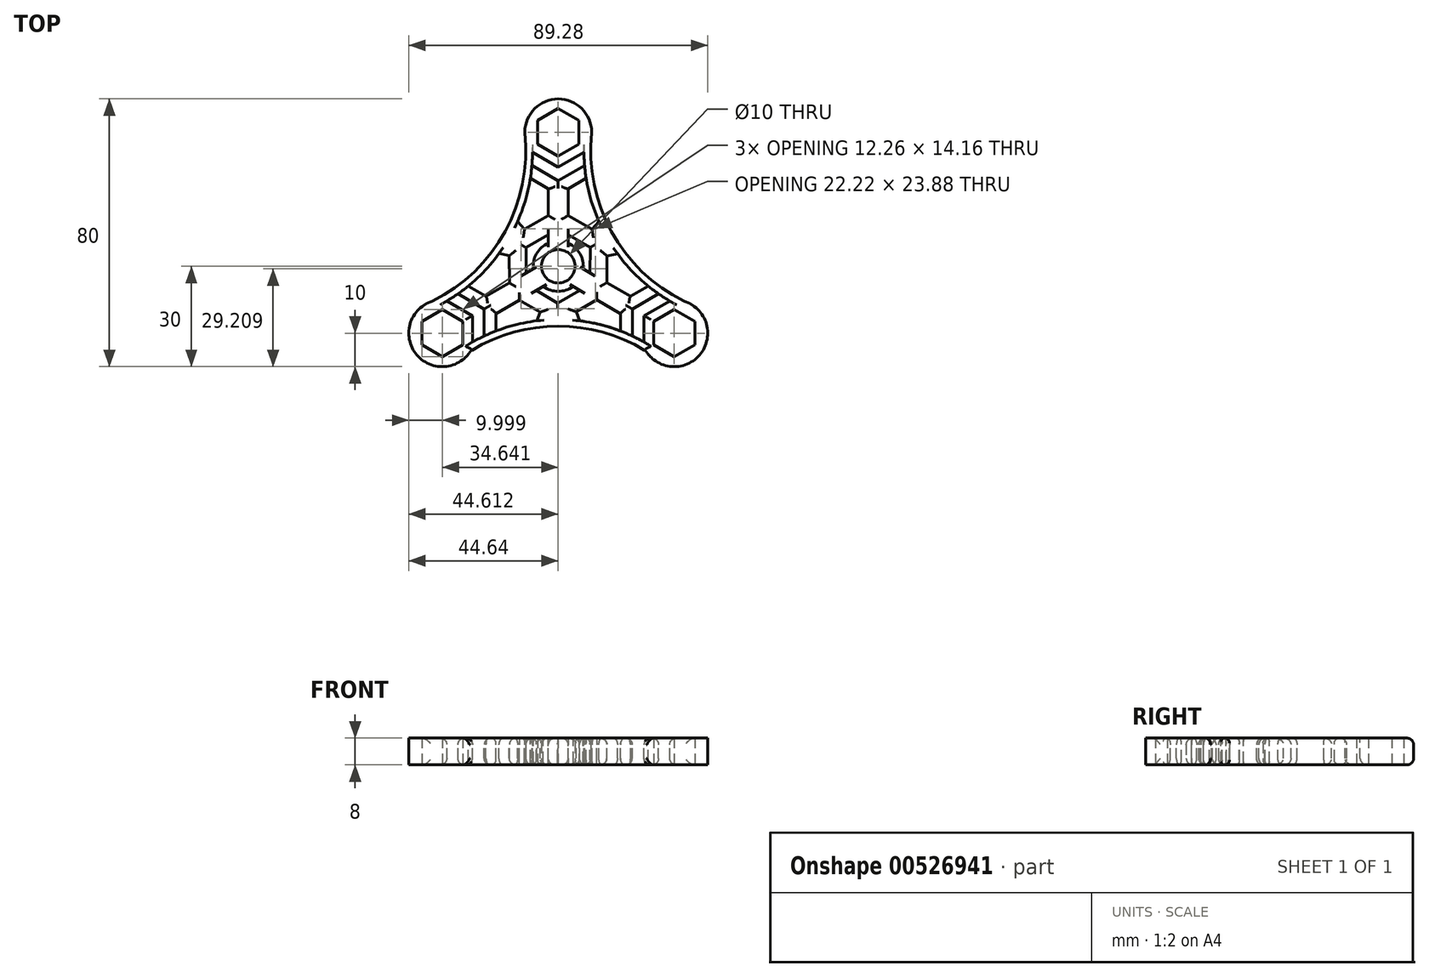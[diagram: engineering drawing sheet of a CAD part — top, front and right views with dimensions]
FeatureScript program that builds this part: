
annotation { "Feature Type Name" : "Feature", "Feature Type Description" : "" }
export const myFeature = defineFeature(function(context is Context, id is Id, definition is map)
    precondition{}
    {
        {
            var Q0;
            Q0=qCreatedBy(makeId("Top.planeOp"),FACE);
            var sketch = newSketch(context, id + "F0", { "sketchPlane" : qUnion([Q0])});
            skCircle(sketch, "E0", {"center": v(0, 0) * mm, "radius": 5 * mm});
            skLineSegment(sketch, "E1.0", {"start": v(-23.24, 13.42) * mm, "end": v(23.24, 13.42) * mm});
            skLineSegment(sketch, "E1.1", {"start": v(23.24, 13.42) * mm, "end": v(0, -26.83) * mm});
            skLineSegment(sketch, "E1.2", {"start": v(0, -26.83) * mm, "end": v(-23.24, 13.42) * mm});
            skPoint(sketch, "E1.0.midPoint", {"position": v(0, 13.42) * mm});
            skLineSegment(sketch, "E2", {"start": v(0, 0) * mm, "end": v(0, 40) * mm});
            skLineSegment(sketch, "E3", {"start": v(0, 0) * mm, "end": v(-34.64, -20) * mm});
            skLineSegment(sketch, "E4", {"start": v(0, 0) * mm, "end": v(34.64, -20) * mm});
            skCircle(sketch, "E5.cCircle", {"center": v(0, 40) * mm, "radius": 6.13 * mm, "construction": true});
            skLineSegment(sketch, "E5.0", {"start": v(-6.13, 36.46) * mm, "end": v(-6.13, 43.54) * mm});
            skLineSegment(sketch, "E5.1", {"start": v(-6.13, 43.54) * mm, "end": v(0, 47.08) * mm});
            skLineSegment(sketch, "E5.2", {"start": v(0, 47.08) * mm, "end": v(6.13, 43.54) * mm});
            skLineSegment(sketch, "E5.3", {"start": v(6.13, 43.54) * mm, "end": v(6.13, 36.46) * mm});
            skLineSegment(sketch, "E5.4", {"start": v(6.13, 36.46) * mm, "end": v(0, 32.92) * mm});
            skLineSegment(sketch, "E5.5", {"start": v(0, 32.92) * mm, "end": v(-6.13, 36.46) * mm});
            skPoint(sketch, "E5.0.midPoint", {"position": v(-6.13, 40) * mm});
            skCircle(sketch, "E6.cCircle", {"center": v(-34.64, -20) * mm, "radius": 6.13 * mm, "construction": true});
            skLineSegment(sketch, "E6.0", {"start": v(-40.77, -23.54) * mm, "end": v(-40.77, -16.46) * mm});
            skLineSegment(sketch, "E6.1", {"start": v(-40.77, -16.46) * mm, "end": v(-34.64, -12.92) * mm});
            skLineSegment(sketch, "E6.2", {"start": v(-34.64, -12.92) * mm, "end": v(-28.51, -16.46) * mm});
            skLineSegment(sketch, "E6.3", {"start": v(-28.51, -16.46) * mm, "end": v(-28.51, -23.54) * mm});
            skLineSegment(sketch, "E6.4", {"start": v(-28.51, -23.54) * mm, "end": v(-34.64, -27.08) * mm});
            skLineSegment(sketch, "E6.5", {"start": v(-34.64, -27.08) * mm, "end": v(-40.77, -23.54) * mm});
            skPoint(sketch, "E6.0.midPoint", {"position": v(-40.77, -20) * mm});
            skCircle(sketch, "E7.cCircle", {"center": v(34.64, -20) * mm, "radius": 6.13 * mm, "construction": true});
            skLineSegment(sketch, "E7.0", {"start": v(40.77, -16.46) * mm, "end": v(40.77, -23.54) * mm});
            skLineSegment(sketch, "E7.1", {"start": v(40.77, -23.54) * mm, "end": v(34.64, -27.08) * mm});
            skLineSegment(sketch, "E7.2", {"start": v(34.64, -27.08) * mm, "end": v(28.51, -23.54) * mm});
            skLineSegment(sketch, "E7.3", {"start": v(28.51, -23.54) * mm, "end": v(28.51, -16.46) * mm});
            skLineSegment(sketch, "E7.4", {"start": v(28.51, -16.46) * mm, "end": v(34.64, -12.92) * mm});
            skLineSegment(sketch, "E7.5", {"start": v(34.64, -12.92) * mm, "end": v(40.77, -16.46) * mm});
            skPoint(sketch, "E7.0.midPoint", {"position": v(40.77, -20) * mm});
            skCircle(sketch, "E8", {"center": v(0, 40) * mm, "radius": 10 * mm});
            skCircle(sketch, "E9", {"center": v(-34.64, -20) * mm, "radius": 10 * mm});
            skCircle(sketch, "E10", {"center": v(34.64, -20) * mm, "radius": 10 * mm});
            skArc(sketch, "E11", {"start": v(-37.7, -10.48) * mm, "mid": v(-15.86, 10.37) * mm, "end": v(-10, 40) * mm});
            skPoint(sketch, "E11.startSnap0", {"position": v(-37.7, -14.7) * mm});
            skPoint(sketch, "E12.startSnap0", {"position": v(31.58, -25.3) * mm});
            skPoint(sketch, "E12.endSnap0", {"position": v(-31.58, -25.3) * mm});
            skArc(sketch, "E13", {"start": v(10, 40) * mm, "mid": v(15.86, 10.37) * mm, "end": v(37.7, -10.48) * mm});
            skPoint(sketch, "E13.startSnap0", {"position": v(6.13, 40) * mm});
            skPoint(sketch, "E13.endSnap0", {"position": v(37.7, -14.7) * mm});
            skArc(sketch, "E14", {"start": v(26.17, -25.3) * mm, "mid": v(0, -17.92) * mm, "end": v(-26.17, -25.3) * mm});
            skSolve(sketch);
        }
        {
            var Q0;
            {var subQ0=sQuery(id+"F0.wireOp",EDGE,"E11");var subQ1=sQuery(id+"F0.wireOp",EDGE,"E1.0");var subQ2=makeQuery(id+"F0.imprint","INTERSECT",VERTEX,{"derivedFrom":[subQ1,subQ0]});Q0=makeQuery(id+"F0.imprint","IMPRINT",FACE,{"disambiguationData":[TD([[makeQuery(id+"F0.imprint","IMPRINT",EDGE,{"disambiguationData":[TD([[subQ2,-1.0]])],"derivedFrom":subQ1}),1.0]])]});}
            var Q1;
            Q1=makeQuery(id+"F0.imprint","IMPRINT",FACE,{"disambiguationData":[TD([[makeQuery(id+"F0.imprint","IMPRINT",EDGE,{"derivedFrom":sQuery(id+"F0.wireOp",EDGE,"E5.0")}),1.0]])]});
            var Q2;
            {var subQ0=sQuery(id+"F0.wireOp",EDGE,"E13");var subQ1=sQuery(id+"F0.wireOp",EDGE,"E1.0");var subQ2=makeQuery(id+"F0.imprint","INTERSECT",VERTEX,{"derivedFrom":[subQ1,subQ0]});Q2=makeQuery(id+"F0.imprint","IMPRINT",FACE,{"disambiguationData":[TD([[makeQuery(id+"F0.imprint","IMPRINT",EDGE,{"disambiguationData":[TD([[subQ2,1.0]])],"derivedFrom":subQ1}),1.0]])]});}
            var Q3;
            {var subQ1=sQuery(id+"F0.wireOp",EDGE,"E0");var subQ8=sQuery(id+"F0.wireOp",EDGE,"E3");var subQ11=makeQuery(id+"F0.imprint","INTERSECT",VERTEX,{"derivedFrom":[subQ1,subQ8]});Q3=makeQuery(id+"F0.imprint","IMPRINT",FACE,{"disambiguationData":[TD([[makeQuery(id+"F0.imprint","IMPRINT",EDGE,{"disambiguationData":[TD([[subQ11,1.0]])],"derivedFrom":subQ1}),-1.0]])]});}
            var Q4;
            {var subQ0=sQuery(id+"F0.wireOp",EDGE,"E2");var subQ1=sQuery(id+"F0.wireOp",EDGE,"E0");var subQ2=makeQuery(id+"F0.imprint","INTERSECT",VERTEX,{"derivedFrom":[subQ1,subQ0]});Q4=makeQuery(id+"F0.imprint","IMPRINT",FACE,{"disambiguationData":[TD([[makeQuery(id+"F0.imprint","IMPRINT",EDGE,{"disambiguationData":[TD([[subQ2,1.0]])],"derivedFrom":subQ1}),-1.0]])]});}
            var Q5;
            {var subQ3=sQuery(id+"F0.wireOp",EDGE,"E3");var subQ5=sQuery(id+"F0.wireOp",EDGE,"E0");var subQ6=makeQuery(id+"F0.imprint","INTERSECT",VERTEX,{"derivedFrom":[subQ5,subQ3]});Q5=makeQuery(id+"F0.imprint","IMPRINT",FACE,{"disambiguationData":[TD([[makeQuery(id+"F0.imprint","IMPRINT",EDGE,{"disambiguationData":[TD([[subQ6,-1.0]])],"derivedFrom":subQ5}),-1.0]])]});}
            var Q6;
            {var subQ0=sQuery(id+"F0.wireOp",EDGE,"E12");var subQ1=sQuery(id+"F0.wireOp",EDGE,"E1.2");var subQ2=makeQuery(id+"F0.imprint","INTERSECT",VERTEX,{"derivedFrom":[subQ1,subQ0]});Q6=makeQuery(id+"F0.imprint","IMPRINT",FACE,{"disambiguationData":[TD([[makeQuery(id+"F0.imprint","IMPRINT",EDGE,{"disambiguationData":[TD([[subQ2,-1.0]])],"derivedFrom":subQ1}),1.0]])]});}
            var Q7;
            {var subQ0=sQuery(id+"F0.wireOp",EDGE,"E11");var subQ1=sQuery(id+"F0.wireOp",EDGE,"E1.2");var subQ2=makeQuery(id+"F0.imprint","INTERSECT",VERTEX,{"derivedFrom":[subQ1,subQ0]});Q7=makeQuery(id+"F0.imprint","IMPRINT",FACE,{"disambiguationData":[TD([[makeQuery(id+"F0.imprint","IMPRINT",EDGE,{"disambiguationData":[TD([[subQ2,1.0]])],"derivedFrom":subQ1}),1.0]])]});}
            var Q8;
            Q8=makeQuery(id+"F0.imprint","IMPRINT",FACE,{"disambiguationData":[TD([[makeQuery(id+"F0.imprint","IMPRINT",EDGE,{"derivedFrom":sQuery(id+"F0.wireOp",EDGE,"E6.0")}),1.0]])]});
            var Q9;
            {var subQ0=sQuery(id+"F0.wireOp",EDGE,"E12");var subQ1=sQuery(id+"F0.wireOp",EDGE,"E1.1");var subQ2=makeQuery(id+"F0.imprint","INTERSECT",VERTEX,{"derivedFrom":[subQ1,subQ0]});Q9=makeQuery(id+"F0.imprint","IMPRINT",FACE,{"disambiguationData":[TD([[makeQuery(id+"F0.imprint","IMPRINT",EDGE,{"disambiguationData":[TD([[subQ2,1.0]])],"derivedFrom":subQ1}),1.0]])]});}
            var Q10;
            {var subQ0=sQuery(id+"F0.wireOp",EDGE,"E13");var subQ1=sQuery(id+"F0.wireOp",EDGE,"E1.1");var subQ2=makeQuery(id+"F0.imprint","INTERSECT",VERTEX,{"derivedFrom":[subQ1,subQ0]});Q10=makeQuery(id+"F0.imprint","IMPRINT",FACE,{"disambiguationData":[TD([[makeQuery(id+"F0.imprint","IMPRINT",EDGE,{"disambiguationData":[TD([[subQ2,-1.0]])],"derivedFrom":subQ1}),1.0]])]});}
            var Q11;
            Q11=makeQuery(id+"F0.imprint","IMPRINT",FACE,{"disambiguationData":[TD([[makeQuery(id+"F0.imprint","IMPRINT",EDGE,{"derivedFrom":sQuery(id+"F0.wireOp",EDGE,"E7.0")}),1.0]])]});
            extrude(context, id + "F1", {"entities" : qUnion([Q0, Q1, Q2, Q3, Q4, Q5, Q6, Q7, Q8, Q9, Q10, Q11]), "depth" : 8 * mm, "offsetDistance" : 25 * mm});
        }
        {
            var Q0;
            Q0=makeQuery(id+"F1.opExtrude","SWEPT_FACE",FACE,{"disambiguationData":[OSD([sQuery(id+"F0.wireOp",EDGE,"E14")])]});
            var Q1;
            Q1=makeQuery(id+"F1.opExtrude","SWEPT_FACE",FACE,{"disambiguationData":[OSD([sQuery(id+"F0.wireOp",EDGE,"E11")])]});
            var Q2;
            Q2=makeQuery(id+"F1.opExtrude","SWEPT_FACE",FACE,{"disambiguationData":[OSD([sQuery(id+"F0.wireOp",EDGE,"E13")])]});
            var Q3;
            Q3=makeQuery(id+"F1.opExtrude","SWEPT_FACE",FACE,{"disambiguationData":[OSD([sQuery(id+"F0.wireOp",EDGE,"E8")])]});
            fillet(context, id + "F2", {"entities" : qUnion([Q0, Q1, Q2, Q3]), "radius" : 2 * mm, "tangentPropagation" : true, "allowEdgeOverflow" : false});
        }
        {
            var Q0;
            Q0=makeQuery(id+"F1.opExtrude","CAP_FACE",FACE,{"disambiguationData":[OSD([sQuery(id+"F0.wireOp",EDGE,"E0"),sQuery(id+"F0.wireOp",EDGE,"E5.0"),sQuery(id+"F0.wireOp",EDGE,"E5.1"),sQuery(id+"F0.wireOp",EDGE,"E5.2"),sQuery(id+"F0.wireOp",EDGE,"E5.3"),sQuery(id+"F0.wireOp",EDGE,"E5.4"),sQuery(id+"F0.wireOp",EDGE,"E5.5"),sQuery(id+"F0.wireOp",EDGE,"E6.0"),sQuery(id+"F0.wireOp",EDGE,"E6.1"),sQuery(id+"F0.wireOp",EDGE,"E6.2"),sQuery(id+"F0.wireOp",EDGE,"E6.3"),sQuery(id+"F0.wireOp",EDGE,"E6.4"),sQuery(id+"F0.wireOp",EDGE,"E6.5"),sQuery(id+"F0.wireOp",EDGE,"E7.0"),sQuery(id+"F0.wireOp",EDGE,"E7.1"),sQuery(id+"F0.wireOp",EDGE,"E7.2"),sQuery(id+"F0.wireOp",EDGE,"E7.3"),sQuery(id+"F0.wireOp",EDGE,"E7.4"),sQuery(id+"F0.wireOp",EDGE,"E7.5"),sQuery(id+"F0.wireOp",EDGE,"E8"),sQuery(id+"F0.wireOp",EDGE,"E9"),sQuery(id+"F0.wireOp",EDGE,"E10"),sQuery(id+"F0.wireOp",EDGE,"E11"),sQuery(id+"F0.wireOp",EDGE,"E13"),sQuery(id+"F0.wireOp",EDGE,"E14")])],"isStart":false});
            var sketch = newSketch(context, id + "F3", { "sketchPlane" : qUnion([Q0])});
            skLineSegment(sketch, "E15.0", {"start": v(6.13, 36.46) * mm, "end": v(0, 32.92) * mm});
            skLineSegment(sketch, "E15.1", {"start": v(0, 32.92) * mm, "end": v(-6.13, 36.46) * mm});
            skLineSegment(sketch, "E16.0", {"start": v(0, 29.57) * mm, "end": v(-7.7, 34.01) * mm});
            skLineSegment(sketch, "E16.1", {"start": v(7.7, 34.01) * mm, "end": v(0, 29.57) * mm});
            skArc(sketch, "E17.0", {"start": v(36.7, -12.21) * mm, "mid": v(14.1, 9.42) * mm, "end": v(8, 40.1) * mm});
            skArc(sketch, "E17.1", {"start": v(-8, 40.1) * mm, "mid": v(-14.1, 9.42) * mm, "end": v(-36.7, -12.21) * mm});
            skLineSegment(sketch, "E18.0", {"start": v(0, 25.53) * mm, "end": v(-7.87, 30.08) * mm});
            skLineSegment(sketch, "E18.1", {"start": v(7.87, 30.08) * mm, "end": v(0, 25.53) * mm});
            skLineSegment(sketch, "E19.0", {"start": v(-3, 23.22) * mm, "end": v(-8.33, 26.3) * mm});
            skLineSegment(sketch, "E19.1", {"start": v(8.33, 26.3) * mm, "end": v(3, 23.22) * mm});
            skLineSegment(sketch, "E20.0", {"start": v(3, 9.42) * mm, "end": v(9.57, 5.65) * mm});
            skLineSegment(sketch, "E20.1", {"start": v(9.57, 5.65) * mm, "end": v(9.5, -2.02) * mm});
            skLineSegment(sketch, "E20.2", {"start": v(9.48, -5.44) * mm, "end": v(9.45, -5.46) * mm});
            skLineSegment(sketch, "E20.3", {"start": v(-0.15, -11) * mm, "end": v(-6.6, -7.27) * mm});
            skLineSegment(sketch, "E20.4", {"start": v(-9.61, -2.09) * mm, "end": v(-9.63, 5.57) * mm});
            skLineSegment(sketch, "E20.5", {"start": v(-9.63, 5.57) * mm, "end": v(-3, 9.4) * mm});
            skLineSegment(sketch, "E21.0", {"start": v(-14.6, -4.97) * mm, "end": v(-14.63, 3.14) * mm});
            skLineSegment(sketch, "E21.1", {"start": v(3, 15.18) * mm, "end": v(10.09, 11.12) * mm});
            skLineSegment(sketch, "E21.2", {"start": v(14.55, 3.08) * mm, "end": v(14.48, -4.9) * mm});
            skLineSegment(sketch, "E21.3", {"start": v(-10.07, 11.1) * mm, "end": v(-3, 15.17) * mm});
            skLineSegment(sketch, "E21.4", {"start": v(11.45, -10.08) * mm, "end": v(5.37, -13.59) * mm});
            skArc(sketch, "E22", {"start": v(-3, 6.87) * mm, "mid": v(-6.5, 3.75) * mm, "end": v(-7.45, -0.84) * mm});
            skLineSegment(sketch, "E23.right", {"start": v(3, 6.87) * mm, "end": v(3, 9.42) * mm});
            skLineSegment(sketch, "E24.right", {"start": v(-3, 6.87) * mm, "end": v(-3, 9.4) * mm});
            skLineSegment(sketch, "E25.trimOffspring", {"start": v(3, 15.18) * mm, "end": v(3, 23.22) * mm});
            skLineSegment(sketch, "E26.trimOffspring", {"start": v(-3, 15.17) * mm, "end": v(-3, 23.22) * mm});
            skLineSegment(sketch, "E27.trimOffspring", {"start": v(0, 25.53) * mm, "end": v(0, 29.57) * mm});
            skLineSegment(sketch, "E28.trimOffspring", {"start": v(0, 25.53) * mm, "end": v(0, 40) * mm});
            skLineSegment(sketch, "E29.trimOffspring", {"start": v(0, 11.13) * mm, "end": v(0, 11.14) * mm});
            skLineSegment(sketch, "E30.0", {"start": v(-25.61, -14.79) * mm, "end": v(-25.61, -22.66) * mm});
            skLineSegment(sketch, "E30.1", {"start": v(-33.27, -10.36) * mm, "end": v(-25.61, -14.79) * mm});
            skLineSegment(sketch, "E31.0", {"start": v(-22.11, -12.77) * mm, "end": v(-22.11, -20.85) * mm});
            skLineSegment(sketch, "E31.1", {"start": v(-29.96, -8.24) * mm, "end": v(-22.11, -12.77) * mm});
            skLineSegment(sketch, "E32.0", {"start": v(-18.61, -10.75) * mm, "end": v(-18.61, -19.36) * mm});
            skLineSegment(sketch, "E32.1", {"start": v(-26.92, -5.95) * mm, "end": v(-18.61, -10.75) * mm});
            skLineSegment(sketch, "E33", {"start": v(-4.45, -6.04) * mm, "end": v(-6.6, -7.27) * mm});
            skLineSegment(sketch, "E34", {"start": v(-7.45, -0.84) * mm, "end": v(-9.61, -2.09) * mm});
            skLineSegment(sketch, "E35.trimOffspring", {"start": v(-25.61, -14.79) * mm, "end": v(-28.51, -16.46) * mm});
            skArc(sketch, "E36.0", {"start": v(-26.8, -23.36) * mm, "mid": v(0, -15.92) * mm, "end": v(26.8, -23.36) * mm});
            skLineSegment(sketch, "E37.trimOffspring", {"start": v(-11.6, -10.16) * mm, "end": v(-18.61, -14.2) * mm});
            skLineSegment(sketch, "E38.trimOffspring", {"start": v(-14.6, -4.97) * mm, "end": v(-21.61, -9.01) * mm});
            skArc(sketch, "E39.trimOffspring", {"start": v(-4.45, -6.04) * mm, "mid": v(0, -7.5) * mm, "end": v(4.45, -6.04) * mm});
            skLineSegment(sketch, "E40.0", {"start": v(28.51, -23.54) * mm, "end": v(28.51, -16.46) * mm});
            skLineSegment(sketch, "E40.1", {"start": v(28.51, -16.46) * mm, "end": v(34.64, -12.92) * mm});
            skLineSegment(sketch, "E41.0", {"start": v(-34.64, -12.92) * mm, "end": v(-28.51, -16.46) * mm});
            skLineSegment(sketch, "E41.1", {"start": v(-28.51, -16.46) * mm, "end": v(-28.51, -23.54) * mm});
            skLineSegment(sketch, "E42.0", {"start": v(25.61, -14.79) * mm, "end": v(33.27, -10.36) * mm});
            skLineSegment(sketch, "E42.1", {"start": v(25.61, -22.66) * mm, "end": v(25.61, -14.79) * mm});
            skLineSegment(sketch, "E43.0", {"start": v(22.11, -12.77) * mm, "end": v(29.96, -8.24) * mm});
            skLineSegment(sketch, "E43.1", {"start": v(22.11, -20.85) * mm, "end": v(22.11, -12.77) * mm});
            skLineSegment(sketch, "E44.0", {"start": v(18.61, -10.75) * mm, "end": v(26.92, -5.95) * mm});
            skLineSegment(sketch, "E44.1", {"start": v(18.61, -19.36) * mm, "end": v(18.61, -10.75) * mm});
            skLineSegment(sketch, "E45", {"start": v(7.45, -0.84) * mm, "end": v(9.5, -2.02) * mm});
            skLineSegment(sketch, "E46", {"start": v(4.45, -6.04) * mm, "end": v(6.45, -7.19) * mm});
            skPoint(sketch, "E47.orphan", {"position": v(-34.64, -20) * mm});
            skPoint(sketch, "E48.trimOffspring.end.orphan", {"position": v(34.64, -20) * mm});
            skLineSegment(sketch, "E49.trimOffspring", {"start": v(18.61, -10.75) * mm, "end": v(22.11, -12.77) * mm});
            skLineSegment(sketch, "E50.trimOffspring", {"start": v(14.48, -4.9) * mm, "end": v(21.61, -9.01) * mm});
            skLineSegment(sketch, "E51.trimOffspring", {"start": v(11.45, -10.08) * mm, "end": v(18.61, -14.2) * mm});
            skLineSegment(sketch, "E52.trimOffspring", {"start": v(6.45, -7.19) * mm, "end": v(-0.15, -11) * mm});
            skArc(sketch, "E53.trimOffspring", {"start": v(7.45, -0.84) * mm, "mid": v(6.5, 3.75) * mm, "end": v(3, 6.87) * mm});
            skLineSegment(sketch, "E54", {"start": v(10.09, 11.12) * mm, "end": v(12.14, 13.38) * mm});
            skLineSegment(sketch, "E55", {"start": v(14.55, 3.08) * mm, "end": v(17.7, 3.75) * mm});
            skPoint(sketch, "E55.endSnap0", {"position": v(6.5, 3.75) * mm});
            skLineSegment(sketch, "E56", {"start": v(5.37, -13.59) * mm, "end": v(6.45, -16.32) * mm});
            skLineSegment(sketch, "E57", {"start": v(-5.43, -13.72) * mm, "end": v(-6.45, -16.32) * mm});
            skLineSegment(sketch, "E58.trimOffspring", {"start": v(-10.07, 11.1) * mm, "end": v(-12.14, 13.38) * mm});
            skLineSegment(sketch, "E59.trimOffspring", {"start": v(-14.63, 3.14) * mm, "end": v(-17.67, 3.8) * mm});
            skLineSegment(sketch, "E60.trimOffspring", {"start": v(-5.43, -13.72) * mm, "end": v(-11.6, -10.16) * mm});
            skSolve(sketch);
        }
        {
            var Q0;
            {var subQ0=sQuery(id+"F3.wireOp",EDGE,"E16.0");Q0=makeQuery(id+"F3.imprint","IMPRINT",FACE,{"disambiguationData":[TD([[makeQuery(id+"F3.imprint","IMPRINT",EDGE,{"derivedFrom":subQ0}),1.0]])]});}
            var Q1;
            {var subQ0=sQuery(id+"F3.wireOp",EDGE,"E16.1");Q1=makeQuery(id+"F3.imprint","IMPRINT",FACE,{"disambiguationData":[TD([[makeQuery(id+"F3.imprint","IMPRINT",EDGE,{"derivedFrom":subQ0}),1.0]])]});}
            var Q2;
            {var subQ0=sQuery(id+"F3.wireOp",EDGE,"E19.1");Q2=makeQuery(id+"F3.imprint","IMPRINT",FACE,{"disambiguationData":[TD([[makeQuery(id+"F3.imprint","IMPRINT",EDGE,{"derivedFrom":subQ0}),1.0]])]});}
            var Q3;
            Q3=makeQuery(id+"F3.imprint","IMPRINT",FACE,{"disambiguationData":[TD([[makeQuery(id+"F3.imprint","IMPRINT",EDGE,{"derivedFrom":sQuery(id+"F3.wireOp",EDGE,"E20.4")}),-1.0]])]});
            var Q4;
            Q4=makeQuery(id+"F3.imprint","IMPRINT",FACE,{"disambiguationData":[TD([[makeQuery(id+"F3.imprint","IMPRINT",EDGE,{"derivedFrom":sQuery(id+"F3.wireOp",EDGE,"E20.0")}),-1.0]])]});
            var Q5;
            Q5=makeQuery(id+"F3.imprint","IMPRINT",FACE,{"disambiguationData":[TD([[makeQuery(id+"F3.imprint","IMPRINT",EDGE,{"derivedFrom":sQuery(id+"F3.wireOp",EDGE,"E20.3")}),-1.0]])]});
            var Q6;
            {var subQ0=sQuery(id+"F3.wireOp",EDGE,"E21.0");Q6=makeQuery(id+"F3.imprint","IMPRINT",FACE,{"disambiguationData":[TD([[makeQuery(id+"F3.imprint","IMPRINT",EDGE,{"derivedFrom":subQ0}),1.0]])]});}
            var Q7;
            {var subQ0=sQuery(id+"F3.wireOp",EDGE,"E37.trimOffspring");Q7=makeQuery(id+"F3.imprint","IMPRINT",FACE,{"disambiguationData":[TD([[makeQuery(id+"F3.imprint","IMPRINT",EDGE,{"derivedFrom":subQ0}),1.0]])]});}
            var Q8;
            {var subQ1=sQuery(id+"F3.wireOp",EDGE,"E42.0");Q8=makeQuery(id+"F3.imprint","IMPRINT",FACE,{"disambiguationData":[TD([[makeQuery(id+"F3.imprint","IMPRINT",EDGE,{"derivedFrom":subQ1}),1.0]])]});}
            var Q9;
            {var subQ0=sQuery(id+"F3.wireOp",EDGE,"E51.trimOffspring");Q9=makeQuery(id+"F3.imprint","IMPRINT",FACE,{"disambiguationData":[TD([[makeQuery(id+"F3.imprint","IMPRINT",EDGE,{"derivedFrom":subQ0}),-1.0]])]});}
            var Q10;
            {var subQ2=sQuery(id+"F3.wireOp",EDGE,"E30.0");Q10=makeQuery(id+"F3.imprint","IMPRINT",FACE,{"disambiguationData":[TD([[makeQuery(id+"F3.imprint","IMPRINT",EDGE,{"derivedFrom":subQ2}),1.0]])]});}
            var Q11;
            {var subQ0=sQuery(id+"F3.wireOp",EDGE,"E19.0");Q11=makeQuery(id+"F3.imprint","IMPRINT",FACE,{"disambiguationData":[TD([[makeQuery(id+"F3.imprint","IMPRINT",EDGE,{"derivedFrom":subQ0}),1.0]])]});}
            var Q12;
            Q12=makeQuery(id+"F3.imprint","IMPRINT",FACE,{"disambiguationData":[TD([[makeQuery(id+"F3.imprint","IMPRINT",EDGE,{"derivedFrom":sQuery(id+"F3.wireOp",EDGE,"E21.2")}),1.0]])]});
            extrude(context, id + "F4", {"entities" : qUnion([Q0, Q1, Q2, Q3, Q4, Q5, Q6, Q7, Q8, Q9, Q10, Q11, Q12]), "operationType" : NewBodyOperationType.REMOVE, "oppositeDirection" : true, "depth" : 10 * mm, "offsetDistance" : 25 * mm});
        }
        {
            var Q0;
            Q0=makeQuery(id+"F4.boolean.opBoolean","COPY",EDGE,{"derivedFrom":makeQuery(id+"F4.opExtrude","CAP_EDGE",EDGE,{"disambiguationData":[OSD([sQuery(id+"F3.wireOp",EDGE,"E16.0")])],"isStart":true})});
            var Q1;
            Q1=makeQuery(id+"F4.boolean.opBoolean","COPY",EDGE,{"derivedFrom":makeQuery(id+"F4.opExtrude","CAP_EDGE",EDGE,{"disambiguationData":[OSD([sQuery(id+"F3.wireOp",EDGE,"E16.1")])],"isStart":true})});
            var Q2;
            Q2=makeQuery(id+"F4.boolean.opBoolean","COPY",EDGE,{"derivedFrom":makeQuery(id+"F4.opExtrude","CAP_EDGE",EDGE,{"disambiguationData":[OSD([sQuery(id+"F3.wireOp",EDGE,"E18.1")])],"isStart":true})});
            var Q3;
            Q3=makeQuery(id+"F4.boolean.opBoolean","COPY",EDGE,{"derivedFrom":makeQuery(id+"F4.opExtrude","CAP_EDGE",EDGE,{"disambiguationData":[OSD([sQuery(id+"F3.wireOp",EDGE,"E18.0")])],"isStart":true})});
            var Q4;
            Q4=makeQuery(id+"F4.boolean.opBoolean","COPY",EDGE,{"derivedFrom":makeQuery(id+"F4.opExtrude","CAP_EDGE",EDGE,{"disambiguationData":[OSD([sQuery(id+"F3.wireOp",EDGE,"E21.1")])],"isStart":true})});
            var Q5;
            Q5=makeQuery(id+"F4.boolean.opBoolean","COPY",EDGE,{"derivedFrom":makeQuery(id+"F4.opExtrude","CAP_EDGE",EDGE,{"disambiguationData":[OSD([sQuery(id+"F3.wireOp",EDGE,"E25.trimOffspring")])],"isStart":true})});
            var Q6;
            Q6=makeQuery(id+"F4.boolean.opBoolean","COPY",EDGE,{"derivedFrom":makeQuery(id+"F4.opExtrude","CAP_EDGE",EDGE,{"disambiguationData":[OSD([sQuery(id+"F3.wireOp",EDGE,"E21.3")])],"isStart":true})});
            var Q7;
            Q7=makeQuery(id+"F4.boolean.opBoolean","COPY",EDGE,{"derivedFrom":makeQuery(id+"F4.opExtrude","CAP_EDGE",EDGE,{"disambiguationData":[OSD([sQuery(id+"F3.wireOp",EDGE,"E26.trimOffspring")])],"isStart":true})});
            var Q8;
            Q8=makeQuery(id+"F4.boolean.opBoolean","COPY",EDGE,{"derivedFrom":makeQuery(id+"F4.opExtrude","CAP_EDGE",EDGE,{"disambiguationData":[OSD([sQuery(id+"F3.wireOp",EDGE,"E30.1")])],"isStart":true})});
            var Q9;
            Q9=makeQuery(id+"F4.boolean.opBoolean","COPY",EDGE,{"derivedFrom":makeQuery(id+"F4.opExtrude","CAP_EDGE",EDGE,{"disambiguationData":[OSD([sQuery(id+"F3.wireOp",EDGE,"E30.0")])],"isStart":true})});
            var Q10;
            Q10=makeQuery(id+"F4.boolean.opBoolean","COPY",EDGE,{"derivedFrom":makeQuery(id+"F4.opExtrude","CAP_EDGE",EDGE,{"disambiguationData":[OSD([sQuery(id+"F3.wireOp",EDGE,"E31.1")])],"isStart":true})});
            var Q11;
            Q11=makeQuery(id+"F4.boolean.opBoolean","COPY",EDGE,{"derivedFrom":makeQuery(id+"F4.opExtrude","CAP_EDGE",EDGE,{"disambiguationData":[OSD([sQuery(id+"F3.wireOp",EDGE,"E31.0")])],"isStart":true})});
            var Q12;
            Q12=makeQuery(id+"F4.boolean.opBoolean","COPY",EDGE,{"derivedFrom":makeQuery(id+"F4.opExtrude","CAP_EDGE",EDGE,{"disambiguationData":[OSD([sQuery(id+"F3.wireOp",EDGE,"E42.1")])],"isStart":true})});
            var Q13;
            Q13=makeQuery(id+"F4.boolean.opBoolean","COPY",EDGE,{"derivedFrom":makeQuery(id+"F4.opExtrude","CAP_EDGE",EDGE,{"disambiguationData":[OSD([sQuery(id+"F3.wireOp",EDGE,"E42.0")])],"isStart":true})});
            var Q14;
            Q14=makeQuery(id+"F4.boolean.opBoolean","COPY",EDGE,{"derivedFrom":makeQuery(id+"F4.opExtrude","CAP_EDGE",EDGE,{"disambiguationData":[OSD([sQuery(id+"F3.wireOp",EDGE,"E43.0")])],"isStart":true})});
            var Q15;
            Q15=makeQuery(id+"F4.boolean.opBoolean","COPY",EDGE,{"derivedFrom":makeQuery(id+"F4.opExtrude","CAP_EDGE",EDGE,{"disambiguationData":[OSD([sQuery(id+"F3.wireOp",EDGE,"E43.1")])],"isStart":true})});
            var Q16;
            Q16=makeQuery(id+"F4.boolean.opBoolean","COPY",EDGE,{"derivedFrom":makeQuery(id+"F4.opExtrude","CAP_EDGE",EDGE,{"disambiguationData":[OSD([sQuery(id+"F3.wireOp",EDGE,"E38.trimOffspring")])],"isStart":true})});
            var Q17;
            Q17=makeQuery(id+"F4.boolean.opBoolean","COPY",EDGE,{"derivedFrom":makeQuery(id+"F4.opExtrude","CAP_EDGE",EDGE,{"disambiguationData":[OSD([sQuery(id+"F3.wireOp",EDGE,"E21.0")])],"isStart":true})});
            var Q18;
            Q18=makeQuery(id+"F4.boolean.opBoolean","COPY",EDGE,{"derivedFrom":makeQuery(id+"F4.opExtrude","CAP_EDGE",EDGE,{"disambiguationData":[OSD([sQuery(id+"F3.wireOp",EDGE,"E37.trimOffspring")])],"isStart":true})});
            var Q19;
            Q19=makeQuery(id+"F4.boolean.opBoolean","COPY",EDGE,{"derivedFrom":makeQuery(id+"F4.opExtrude","CAP_EDGE",EDGE,{"disambiguationData":[OSD([sQuery(id+"F3.wireOp",EDGE,"E60.trimOffspring")])],"isStart":true})});
            var Q20;
            Q20=makeQuery(id+"F4.boolean.opBoolean","COPY",EDGE,{"derivedFrom":makeQuery(id+"F4.opExtrude","CAP_EDGE",EDGE,{"disambiguationData":[OSD([sQuery(id+"F3.wireOp",EDGE,"E21.4")])],"isStart":true})});
            var Q21;
            Q21=makeQuery(id+"F4.boolean.opBoolean","COPY",EDGE,{"derivedFrom":makeQuery(id+"F4.opExtrude","CAP_EDGE",EDGE,{"disambiguationData":[OSD([sQuery(id+"F3.wireOp",EDGE,"E51.trimOffspring")])],"isStart":true})});
            var Q22;
            Q22=makeQuery(id+"F4.boolean.opBoolean","COPY",EDGE,{"derivedFrom":makeQuery(id+"F4.opExtrude","CAP_EDGE",EDGE,{"disambiguationData":[OSD([sQuery(id+"F3.wireOp",EDGE,"E50.trimOffspring")])],"isStart":true})});
            var Q23;
            Q23=makeQuery(id+"F4.boolean.opBoolean","COPY",EDGE,{"derivedFrom":makeQuery(id+"F4.opExtrude","CAP_EDGE",EDGE,{"disambiguationData":[OSD([sQuery(id+"F3.wireOp",EDGE,"E21.2")])],"isStart":true})});
            var Q24;
            Q24=makeQuery(id+"F4.boolean.opBoolean","COPY",EDGE,{"derivedFrom":makeQuery(id+"F4.opExtrude","CAP_EDGE",EDGE,{"disambiguationData":[OSD([sQuery(id+"F3.wireOp",EDGE,"E55")])],"isStart":true})});
            var Q25;
            Q25=makeQuery(id+"F4.boolean.opBoolean","COPY",EDGE,{"derivedFrom":makeQuery(id+"F4.opExtrude","CAP_EDGE",EDGE,{"disambiguationData":[OSD([sQuery(id+"F3.wireOp",EDGE,"E54")])],"isStart":true})});
            var Q26;
            Q26=makeQuery(id+"F4.boolean.opBoolean","COPY",EDGE,{"derivedFrom":makeQuery(id+"F4.opExtrude","CAP_EDGE",EDGE,{"disambiguationData":[OSD([sQuery(id+"F3.wireOp",EDGE,"E58.trimOffspring")])],"isStart":true})});
            var Q27;
            Q27=makeQuery(id+"F4.boolean.opBoolean","COPY",EDGE,{"derivedFrom":makeQuery(id+"F4.opExtrude","CAP_EDGE",EDGE,{"disambiguationData":[OSD([sQuery(id+"F3.wireOp",EDGE,"E59.trimOffspring")])],"isStart":true})});
            var Q28;
            Q28=makeQuery(id+"F4.boolean.opBoolean","COPY",EDGE,{"derivedFrom":makeQuery(id+"F4.opExtrude","CAP_EDGE",EDGE,{"disambiguationData":[OSD([sQuery(id+"F3.wireOp",EDGE,"E57")])],"isStart":true})});
            var Q29;
            Q29=makeQuery(id+"F4.boolean.opBoolean","COPY",EDGE,{"derivedFrom":makeQuery(id+"F4.opExtrude","CAP_EDGE",EDGE,{"disambiguationData":[OSD([sQuery(id+"F3.wireOp",EDGE,"E56")])],"isStart":true})});
            var Q30;
            Q30=makeQuery(id+"F4.boolean.opBoolean","INTERSECT",EDGE,{"derivedFrom":[makeQuery(id+"F1.opExtrude","CAP_FACE",FACE,{"disambiguationData":[OSD([sQuery(id+"F0.wireOp",EDGE,"E0"),sQuery(id+"F0.wireOp",EDGE,"E5.0"),sQuery(id+"F0.wireOp",EDGE,"E5.1"),sQuery(id+"F0.wireOp",EDGE,"E5.2"),sQuery(id+"F0.wireOp",EDGE,"E5.3"),sQuery(id+"F0.wireOp",EDGE,"E5.4"),sQuery(id+"F0.wireOp",EDGE,"E5.5"),sQuery(id+"F0.wireOp",EDGE,"E6.0"),sQuery(id+"F0.wireOp",EDGE,"E6.1"),sQuery(id+"F0.wireOp",EDGE,"E6.2"),sQuery(id+"F0.wireOp",EDGE,"E6.3"),sQuery(id+"F0.wireOp",EDGE,"E6.4"),sQuery(id+"F0.wireOp",EDGE,"E6.5"),sQuery(id+"F0.wireOp",EDGE,"E7.0"),sQuery(id+"F0.wireOp",EDGE,"E7.1"),sQuery(id+"F0.wireOp",EDGE,"E7.2"),sQuery(id+"F0.wireOp",EDGE,"E7.3"),sQuery(id+"F0.wireOp",EDGE,"E7.4"),sQuery(id+"F0.wireOp",EDGE,"E7.5"),sQuery(id+"F0.wireOp",EDGE,"E8"),sQuery(id+"F0.wireOp",EDGE,"E9"),sQuery(id+"F0.wireOp",EDGE,"E10"),sQuery(id+"F0.wireOp",EDGE,"E11"),sQuery(id+"F0.wireOp",EDGE,"E13"),sQuery(id+"F0.wireOp",EDGE,"E14")])],"isStart":true}),makeQuery(id+"F4.opExtrude","SWEPT_FACE",FACE,{"disambiguationData":[OSD([sQuery(id+"F3.wireOp",EDGE,"E30.1")])]})]});
            var Q31;
            Q31=makeQuery(id+"F4.boolean.opBoolean","INTERSECT",EDGE,{"derivedFrom":[makeQuery(id+"F1.opExtrude","CAP_FACE",FACE,{"disambiguationData":[OSD([sQuery(id+"F0.wireOp",EDGE,"E0"),sQuery(id+"F0.wireOp",EDGE,"E5.0"),sQuery(id+"F0.wireOp",EDGE,"E5.1"),sQuery(id+"F0.wireOp",EDGE,"E5.2"),sQuery(id+"F0.wireOp",EDGE,"E5.3"),sQuery(id+"F0.wireOp",EDGE,"E5.4"),sQuery(id+"F0.wireOp",EDGE,"E5.5"),sQuery(id+"F0.wireOp",EDGE,"E6.0"),sQuery(id+"F0.wireOp",EDGE,"E6.1"),sQuery(id+"F0.wireOp",EDGE,"E6.2"),sQuery(id+"F0.wireOp",EDGE,"E6.3"),sQuery(id+"F0.wireOp",EDGE,"E6.4"),sQuery(id+"F0.wireOp",EDGE,"E6.5"),sQuery(id+"F0.wireOp",EDGE,"E7.0"),sQuery(id+"F0.wireOp",EDGE,"E7.1"),sQuery(id+"F0.wireOp",EDGE,"E7.2"),sQuery(id+"F0.wireOp",EDGE,"E7.3"),sQuery(id+"F0.wireOp",EDGE,"E7.4"),sQuery(id+"F0.wireOp",EDGE,"E7.5"),sQuery(id+"F0.wireOp",EDGE,"E8"),sQuery(id+"F0.wireOp",EDGE,"E9"),sQuery(id+"F0.wireOp",EDGE,"E10"),sQuery(id+"F0.wireOp",EDGE,"E11"),sQuery(id+"F0.wireOp",EDGE,"E13"),sQuery(id+"F0.wireOp",EDGE,"E14")])],"isStart":true}),makeQuery(id+"F4.opExtrude","SWEPT_FACE",FACE,{"disambiguationData":[OSD([sQuery(id+"F3.wireOp",EDGE,"E30.0")])]})]});
            var Q32;
            Q32=makeQuery(id+"F4.boolean.opBoolean","INTERSECT",EDGE,{"derivedFrom":[makeQuery(id+"F1.opExtrude","CAP_FACE",FACE,{"disambiguationData":[OSD([sQuery(id+"F0.wireOp",EDGE,"E0"),sQuery(id+"F0.wireOp",EDGE,"E5.0"),sQuery(id+"F0.wireOp",EDGE,"E5.1"),sQuery(id+"F0.wireOp",EDGE,"E5.2"),sQuery(id+"F0.wireOp",EDGE,"E5.3"),sQuery(id+"F0.wireOp",EDGE,"E5.4"),sQuery(id+"F0.wireOp",EDGE,"E5.5"),sQuery(id+"F0.wireOp",EDGE,"E6.0"),sQuery(id+"F0.wireOp",EDGE,"E6.1"),sQuery(id+"F0.wireOp",EDGE,"E6.2"),sQuery(id+"F0.wireOp",EDGE,"E6.3"),sQuery(id+"F0.wireOp",EDGE,"E6.4"),sQuery(id+"F0.wireOp",EDGE,"E6.5"),sQuery(id+"F0.wireOp",EDGE,"E7.0"),sQuery(id+"F0.wireOp",EDGE,"E7.1"),sQuery(id+"F0.wireOp",EDGE,"E7.2"),sQuery(id+"F0.wireOp",EDGE,"E7.3"),sQuery(id+"F0.wireOp",EDGE,"E7.4"),sQuery(id+"F0.wireOp",EDGE,"E7.5"),sQuery(id+"F0.wireOp",EDGE,"E8"),sQuery(id+"F0.wireOp",EDGE,"E9"),sQuery(id+"F0.wireOp",EDGE,"E10"),sQuery(id+"F0.wireOp",EDGE,"E11"),sQuery(id+"F0.wireOp",EDGE,"E13"),sQuery(id+"F0.wireOp",EDGE,"E14")])],"isStart":true}),makeQuery(id+"F4.opExtrude","SWEPT_FACE",FACE,{"disambiguationData":[OSD([sQuery(id+"F3.wireOp",EDGE,"E31.0")])]})]});
            var Q33;
            Q33=makeQuery(id+"F4.boolean.opBoolean","INTERSECT",EDGE,{"derivedFrom":[makeQuery(id+"F1.opExtrude","CAP_FACE",FACE,{"disambiguationData":[OSD([sQuery(id+"F0.wireOp",EDGE,"E0"),sQuery(id+"F0.wireOp",EDGE,"E5.0"),sQuery(id+"F0.wireOp",EDGE,"E5.1"),sQuery(id+"F0.wireOp",EDGE,"E5.2"),sQuery(id+"F0.wireOp",EDGE,"E5.3"),sQuery(id+"F0.wireOp",EDGE,"E5.4"),sQuery(id+"F0.wireOp",EDGE,"E5.5"),sQuery(id+"F0.wireOp",EDGE,"E6.0"),sQuery(id+"F0.wireOp",EDGE,"E6.1"),sQuery(id+"F0.wireOp",EDGE,"E6.2"),sQuery(id+"F0.wireOp",EDGE,"E6.3"),sQuery(id+"F0.wireOp",EDGE,"E6.4"),sQuery(id+"F0.wireOp",EDGE,"E6.5"),sQuery(id+"F0.wireOp",EDGE,"E7.0"),sQuery(id+"F0.wireOp",EDGE,"E7.1"),sQuery(id+"F0.wireOp",EDGE,"E7.2"),sQuery(id+"F0.wireOp",EDGE,"E7.3"),sQuery(id+"F0.wireOp",EDGE,"E7.4"),sQuery(id+"F0.wireOp",EDGE,"E7.5"),sQuery(id+"F0.wireOp",EDGE,"E8"),sQuery(id+"F0.wireOp",EDGE,"E9"),sQuery(id+"F0.wireOp",EDGE,"E10"),sQuery(id+"F0.wireOp",EDGE,"E11"),sQuery(id+"F0.wireOp",EDGE,"E13"),sQuery(id+"F0.wireOp",EDGE,"E14")])],"isStart":true}),makeQuery(id+"F4.opExtrude","SWEPT_FACE",FACE,{"disambiguationData":[OSD([sQuery(id+"F3.wireOp",EDGE,"E31.1")])]})]});
            var Q34;
            Q34=makeQuery(id+"F4.boolean.opBoolean","INTERSECT",EDGE,{"derivedFrom":[makeQuery(id+"F1.opExtrude","CAP_FACE",FACE,{"disambiguationData":[OSD([sQuery(id+"F0.wireOp",EDGE,"E0"),sQuery(id+"F0.wireOp",EDGE,"E5.0"),sQuery(id+"F0.wireOp",EDGE,"E5.1"),sQuery(id+"F0.wireOp",EDGE,"E5.2"),sQuery(id+"F0.wireOp",EDGE,"E5.3"),sQuery(id+"F0.wireOp",EDGE,"E5.4"),sQuery(id+"F0.wireOp",EDGE,"E5.5"),sQuery(id+"F0.wireOp",EDGE,"E6.0"),sQuery(id+"F0.wireOp",EDGE,"E6.1"),sQuery(id+"F0.wireOp",EDGE,"E6.2"),sQuery(id+"F0.wireOp",EDGE,"E6.3"),sQuery(id+"F0.wireOp",EDGE,"E6.4"),sQuery(id+"F0.wireOp",EDGE,"E6.5"),sQuery(id+"F0.wireOp",EDGE,"E7.0"),sQuery(id+"F0.wireOp",EDGE,"E7.1"),sQuery(id+"F0.wireOp",EDGE,"E7.2"),sQuery(id+"F0.wireOp",EDGE,"E7.3"),sQuery(id+"F0.wireOp",EDGE,"E7.4"),sQuery(id+"F0.wireOp",EDGE,"E7.5"),sQuery(id+"F0.wireOp",EDGE,"E8"),sQuery(id+"F0.wireOp",EDGE,"E9"),sQuery(id+"F0.wireOp",EDGE,"E10"),sQuery(id+"F0.wireOp",EDGE,"E11"),sQuery(id+"F0.wireOp",EDGE,"E13"),sQuery(id+"F0.wireOp",EDGE,"E14")])],"isStart":true}),makeQuery(id+"F4.opExtrude","SWEPT_FACE",FACE,{"disambiguationData":[OSD([sQuery(id+"F3.wireOp",EDGE,"E38.trimOffspring")])]})]});
            var Q35;
            Q35=makeQuery(id+"F4.boolean.opBoolean","INTERSECT",EDGE,{"derivedFrom":[makeQuery(id+"F1.opExtrude","CAP_FACE",FACE,{"disambiguationData":[OSD([sQuery(id+"F0.wireOp",EDGE,"E0"),sQuery(id+"F0.wireOp",EDGE,"E5.0"),sQuery(id+"F0.wireOp",EDGE,"E5.1"),sQuery(id+"F0.wireOp",EDGE,"E5.2"),sQuery(id+"F0.wireOp",EDGE,"E5.3"),sQuery(id+"F0.wireOp",EDGE,"E5.4"),sQuery(id+"F0.wireOp",EDGE,"E5.5"),sQuery(id+"F0.wireOp",EDGE,"E6.0"),sQuery(id+"F0.wireOp",EDGE,"E6.1"),sQuery(id+"F0.wireOp",EDGE,"E6.2"),sQuery(id+"F0.wireOp",EDGE,"E6.3"),sQuery(id+"F0.wireOp",EDGE,"E6.4"),sQuery(id+"F0.wireOp",EDGE,"E6.5"),sQuery(id+"F0.wireOp",EDGE,"E7.0"),sQuery(id+"F0.wireOp",EDGE,"E7.1"),sQuery(id+"F0.wireOp",EDGE,"E7.2"),sQuery(id+"F0.wireOp",EDGE,"E7.3"),sQuery(id+"F0.wireOp",EDGE,"E7.4"),sQuery(id+"F0.wireOp",EDGE,"E7.5"),sQuery(id+"F0.wireOp",EDGE,"E8"),sQuery(id+"F0.wireOp",EDGE,"E9"),sQuery(id+"F0.wireOp",EDGE,"E10"),sQuery(id+"F0.wireOp",EDGE,"E11"),sQuery(id+"F0.wireOp",EDGE,"E13"),sQuery(id+"F0.wireOp",EDGE,"E14")])],"isStart":true}),makeQuery(id+"F4.opExtrude","SWEPT_FACE",FACE,{"disambiguationData":[OSD([sQuery(id+"F3.wireOp",EDGE,"E21.0")])]})]});
            var Q36;
            Q36=makeQuery(id+"F4.boolean.opBoolean","INTERSECT",EDGE,{"derivedFrom":[makeQuery(id+"F1.opExtrude","CAP_FACE",FACE,{"disambiguationData":[OSD([sQuery(id+"F0.wireOp",EDGE,"E0"),sQuery(id+"F0.wireOp",EDGE,"E5.0"),sQuery(id+"F0.wireOp",EDGE,"E5.1"),sQuery(id+"F0.wireOp",EDGE,"E5.2"),sQuery(id+"F0.wireOp",EDGE,"E5.3"),sQuery(id+"F0.wireOp",EDGE,"E5.4"),sQuery(id+"F0.wireOp",EDGE,"E5.5"),sQuery(id+"F0.wireOp",EDGE,"E6.0"),sQuery(id+"F0.wireOp",EDGE,"E6.1"),sQuery(id+"F0.wireOp",EDGE,"E6.2"),sQuery(id+"F0.wireOp",EDGE,"E6.3"),sQuery(id+"F0.wireOp",EDGE,"E6.4"),sQuery(id+"F0.wireOp",EDGE,"E6.5"),sQuery(id+"F0.wireOp",EDGE,"E7.0"),sQuery(id+"F0.wireOp",EDGE,"E7.1"),sQuery(id+"F0.wireOp",EDGE,"E7.2"),sQuery(id+"F0.wireOp",EDGE,"E7.3"),sQuery(id+"F0.wireOp",EDGE,"E7.4"),sQuery(id+"F0.wireOp",EDGE,"E7.5"),sQuery(id+"F0.wireOp",EDGE,"E8"),sQuery(id+"F0.wireOp",EDGE,"E9"),sQuery(id+"F0.wireOp",EDGE,"E10"),sQuery(id+"F0.wireOp",EDGE,"E11"),sQuery(id+"F0.wireOp",EDGE,"E13"),sQuery(id+"F0.wireOp",EDGE,"E14")])],"isStart":true}),makeQuery(id+"F4.opExtrude","SWEPT_FACE",FACE,{"disambiguationData":[OSD([sQuery(id+"F3.wireOp",EDGE,"E59.trimOffspring")])]})]});
            var Q37;
            Q37=makeQuery(id+"F4.boolean.opBoolean","INTERSECT",EDGE,{"derivedFrom":[makeQuery(id+"F1.opExtrude","CAP_FACE",FACE,{"disambiguationData":[OSD([sQuery(id+"F0.wireOp",EDGE,"E0"),sQuery(id+"F0.wireOp",EDGE,"E5.0"),sQuery(id+"F0.wireOp",EDGE,"E5.1"),sQuery(id+"F0.wireOp",EDGE,"E5.2"),sQuery(id+"F0.wireOp",EDGE,"E5.3"),sQuery(id+"F0.wireOp",EDGE,"E5.4"),sQuery(id+"F0.wireOp",EDGE,"E5.5"),sQuery(id+"F0.wireOp",EDGE,"E6.0"),sQuery(id+"F0.wireOp",EDGE,"E6.1"),sQuery(id+"F0.wireOp",EDGE,"E6.2"),sQuery(id+"F0.wireOp",EDGE,"E6.3"),sQuery(id+"F0.wireOp",EDGE,"E6.4"),sQuery(id+"F0.wireOp",EDGE,"E6.5"),sQuery(id+"F0.wireOp",EDGE,"E7.0"),sQuery(id+"F0.wireOp",EDGE,"E7.1"),sQuery(id+"F0.wireOp",EDGE,"E7.2"),sQuery(id+"F0.wireOp",EDGE,"E7.3"),sQuery(id+"F0.wireOp",EDGE,"E7.4"),sQuery(id+"F0.wireOp",EDGE,"E7.5"),sQuery(id+"F0.wireOp",EDGE,"E8"),sQuery(id+"F0.wireOp",EDGE,"E9"),sQuery(id+"F0.wireOp",EDGE,"E10"),sQuery(id+"F0.wireOp",EDGE,"E11"),sQuery(id+"F0.wireOp",EDGE,"E13"),sQuery(id+"F0.wireOp",EDGE,"E14")])],"isStart":true}),makeQuery(id+"F4.opExtrude","SWEPT_FACE",FACE,{"disambiguationData":[OSD([sQuery(id+"F3.wireOp",EDGE,"E37.trimOffspring")])]})]});
            var Q38;
            Q38=makeQuery(id+"F4.boolean.opBoolean","INTERSECT",EDGE,{"derivedFrom":[makeQuery(id+"F1.opExtrude","CAP_FACE",FACE,{"disambiguationData":[OSD([sQuery(id+"F0.wireOp",EDGE,"E0"),sQuery(id+"F0.wireOp",EDGE,"E5.0"),sQuery(id+"F0.wireOp",EDGE,"E5.1"),sQuery(id+"F0.wireOp",EDGE,"E5.2"),sQuery(id+"F0.wireOp",EDGE,"E5.3"),sQuery(id+"F0.wireOp",EDGE,"E5.4"),sQuery(id+"F0.wireOp",EDGE,"E5.5"),sQuery(id+"F0.wireOp",EDGE,"E6.0"),sQuery(id+"F0.wireOp",EDGE,"E6.1"),sQuery(id+"F0.wireOp",EDGE,"E6.2"),sQuery(id+"F0.wireOp",EDGE,"E6.3"),sQuery(id+"F0.wireOp",EDGE,"E6.4"),sQuery(id+"F0.wireOp",EDGE,"E6.5"),sQuery(id+"F0.wireOp",EDGE,"E7.0"),sQuery(id+"F0.wireOp",EDGE,"E7.1"),sQuery(id+"F0.wireOp",EDGE,"E7.2"),sQuery(id+"F0.wireOp",EDGE,"E7.3"),sQuery(id+"F0.wireOp",EDGE,"E7.4"),sQuery(id+"F0.wireOp",EDGE,"E7.5"),sQuery(id+"F0.wireOp",EDGE,"E8"),sQuery(id+"F0.wireOp",EDGE,"E9"),sQuery(id+"F0.wireOp",EDGE,"E10"),sQuery(id+"F0.wireOp",EDGE,"E11"),sQuery(id+"F0.wireOp",EDGE,"E13"),sQuery(id+"F0.wireOp",EDGE,"E14")])],"isStart":true}),makeQuery(id+"F4.opExtrude","SWEPT_FACE",FACE,{"disambiguationData":[OSD([sQuery(id+"F3.wireOp",EDGE,"E60.trimOffspring")])]})]});
            var Q39;
            Q39=makeQuery(id+"F4.boolean.opBoolean","INTERSECT",EDGE,{"derivedFrom":[makeQuery(id+"F1.opExtrude","CAP_FACE",FACE,{"disambiguationData":[OSD([sQuery(id+"F0.wireOp",EDGE,"E0"),sQuery(id+"F0.wireOp",EDGE,"E5.0"),sQuery(id+"F0.wireOp",EDGE,"E5.1"),sQuery(id+"F0.wireOp",EDGE,"E5.2"),sQuery(id+"F0.wireOp",EDGE,"E5.3"),sQuery(id+"F0.wireOp",EDGE,"E5.4"),sQuery(id+"F0.wireOp",EDGE,"E5.5"),sQuery(id+"F0.wireOp",EDGE,"E6.0"),sQuery(id+"F0.wireOp",EDGE,"E6.1"),sQuery(id+"F0.wireOp",EDGE,"E6.2"),sQuery(id+"F0.wireOp",EDGE,"E6.3"),sQuery(id+"F0.wireOp",EDGE,"E6.4"),sQuery(id+"F0.wireOp",EDGE,"E6.5"),sQuery(id+"F0.wireOp",EDGE,"E7.0"),sQuery(id+"F0.wireOp",EDGE,"E7.1"),sQuery(id+"F0.wireOp",EDGE,"E7.2"),sQuery(id+"F0.wireOp",EDGE,"E7.3"),sQuery(id+"F0.wireOp",EDGE,"E7.4"),sQuery(id+"F0.wireOp",EDGE,"E7.5"),sQuery(id+"F0.wireOp",EDGE,"E8"),sQuery(id+"F0.wireOp",EDGE,"E9"),sQuery(id+"F0.wireOp",EDGE,"E10"),sQuery(id+"F0.wireOp",EDGE,"E11"),sQuery(id+"F0.wireOp",EDGE,"E13"),sQuery(id+"F0.wireOp",EDGE,"E14")])],"isStart":true}),makeQuery(id+"F4.opExtrude","SWEPT_FACE",FACE,{"disambiguationData":[OSD([sQuery(id+"F3.wireOp",EDGE,"E57")])]})]});
            var Q40;
            Q40=makeQuery(id+"F4.boolean.opBoolean","INTERSECT",EDGE,{"derivedFrom":[makeQuery(id+"F1.opExtrude","CAP_FACE",FACE,{"disambiguationData":[OSD([sQuery(id+"F0.wireOp",EDGE,"E0"),sQuery(id+"F0.wireOp",EDGE,"E5.0"),sQuery(id+"F0.wireOp",EDGE,"E5.1"),sQuery(id+"F0.wireOp",EDGE,"E5.2"),sQuery(id+"F0.wireOp",EDGE,"E5.3"),sQuery(id+"F0.wireOp",EDGE,"E5.4"),sQuery(id+"F0.wireOp",EDGE,"E5.5"),sQuery(id+"F0.wireOp",EDGE,"E6.0"),sQuery(id+"F0.wireOp",EDGE,"E6.1"),sQuery(id+"F0.wireOp",EDGE,"E6.2"),sQuery(id+"F0.wireOp",EDGE,"E6.3"),sQuery(id+"F0.wireOp",EDGE,"E6.4"),sQuery(id+"F0.wireOp",EDGE,"E6.5"),sQuery(id+"F0.wireOp",EDGE,"E7.0"),sQuery(id+"F0.wireOp",EDGE,"E7.1"),sQuery(id+"F0.wireOp",EDGE,"E7.2"),sQuery(id+"F0.wireOp",EDGE,"E7.3"),sQuery(id+"F0.wireOp",EDGE,"E7.4"),sQuery(id+"F0.wireOp",EDGE,"E7.5"),sQuery(id+"F0.wireOp",EDGE,"E8"),sQuery(id+"F0.wireOp",EDGE,"E9"),sQuery(id+"F0.wireOp",EDGE,"E10"),sQuery(id+"F0.wireOp",EDGE,"E11"),sQuery(id+"F0.wireOp",EDGE,"E13"),sQuery(id+"F0.wireOp",EDGE,"E14")])],"isStart":true}),makeQuery(id+"F4.opExtrude","SWEPT_FACE",FACE,{"disambiguationData":[OSD([sQuery(id+"F3.wireOp",EDGE,"E42.1")])]})]});
            var Q41;
            Q41=makeQuery(id+"F4.boolean.opBoolean","INTERSECT",EDGE,{"derivedFrom":[makeQuery(id+"F1.opExtrude","CAP_FACE",FACE,{"disambiguationData":[OSD([sQuery(id+"F0.wireOp",EDGE,"E0"),sQuery(id+"F0.wireOp",EDGE,"E5.0"),sQuery(id+"F0.wireOp",EDGE,"E5.1"),sQuery(id+"F0.wireOp",EDGE,"E5.2"),sQuery(id+"F0.wireOp",EDGE,"E5.3"),sQuery(id+"F0.wireOp",EDGE,"E5.4"),sQuery(id+"F0.wireOp",EDGE,"E5.5"),sQuery(id+"F0.wireOp",EDGE,"E6.0"),sQuery(id+"F0.wireOp",EDGE,"E6.1"),sQuery(id+"F0.wireOp",EDGE,"E6.2"),sQuery(id+"F0.wireOp",EDGE,"E6.3"),sQuery(id+"F0.wireOp",EDGE,"E6.4"),sQuery(id+"F0.wireOp",EDGE,"E6.5"),sQuery(id+"F0.wireOp",EDGE,"E7.0"),sQuery(id+"F0.wireOp",EDGE,"E7.1"),sQuery(id+"F0.wireOp",EDGE,"E7.2"),sQuery(id+"F0.wireOp",EDGE,"E7.3"),sQuery(id+"F0.wireOp",EDGE,"E7.4"),sQuery(id+"F0.wireOp",EDGE,"E7.5"),sQuery(id+"F0.wireOp",EDGE,"E8"),sQuery(id+"F0.wireOp",EDGE,"E9"),sQuery(id+"F0.wireOp",EDGE,"E10"),sQuery(id+"F0.wireOp",EDGE,"E11"),sQuery(id+"F0.wireOp",EDGE,"E13"),sQuery(id+"F0.wireOp",EDGE,"E14")])],"isStart":true}),makeQuery(id+"F4.opExtrude","SWEPT_FACE",FACE,{"disambiguationData":[OSD([sQuery(id+"F3.wireOp",EDGE,"E42.0")])]})]});
            var Q42;
            Q42=makeQuery(id+"F4.boolean.opBoolean","INTERSECT",EDGE,{"derivedFrom":[makeQuery(id+"F1.opExtrude","CAP_FACE",FACE,{"disambiguationData":[OSD([sQuery(id+"F0.wireOp",EDGE,"E0"),sQuery(id+"F0.wireOp",EDGE,"E5.0"),sQuery(id+"F0.wireOp",EDGE,"E5.1"),sQuery(id+"F0.wireOp",EDGE,"E5.2"),sQuery(id+"F0.wireOp",EDGE,"E5.3"),sQuery(id+"F0.wireOp",EDGE,"E5.4"),sQuery(id+"F0.wireOp",EDGE,"E5.5"),sQuery(id+"F0.wireOp",EDGE,"E6.0"),sQuery(id+"F0.wireOp",EDGE,"E6.1"),sQuery(id+"F0.wireOp",EDGE,"E6.2"),sQuery(id+"F0.wireOp",EDGE,"E6.3"),sQuery(id+"F0.wireOp",EDGE,"E6.4"),sQuery(id+"F0.wireOp",EDGE,"E6.5"),sQuery(id+"F0.wireOp",EDGE,"E7.0"),sQuery(id+"F0.wireOp",EDGE,"E7.1"),sQuery(id+"F0.wireOp",EDGE,"E7.2"),sQuery(id+"F0.wireOp",EDGE,"E7.3"),sQuery(id+"F0.wireOp",EDGE,"E7.4"),sQuery(id+"F0.wireOp",EDGE,"E7.5"),sQuery(id+"F0.wireOp",EDGE,"E8"),sQuery(id+"F0.wireOp",EDGE,"E9"),sQuery(id+"F0.wireOp",EDGE,"E10"),sQuery(id+"F0.wireOp",EDGE,"E11"),sQuery(id+"F0.wireOp",EDGE,"E13"),sQuery(id+"F0.wireOp",EDGE,"E14")])],"isStart":true}),makeQuery(id+"F4.opExtrude","SWEPT_FACE",FACE,{"disambiguationData":[OSD([sQuery(id+"F3.wireOp",EDGE,"E43.1")])]})]});
            var Q43;
            Q43=makeQuery(id+"F4.boolean.opBoolean","INTERSECT",EDGE,{"derivedFrom":[makeQuery(id+"F1.opExtrude","CAP_FACE",FACE,{"disambiguationData":[OSD([sQuery(id+"F0.wireOp",EDGE,"E0"),sQuery(id+"F0.wireOp",EDGE,"E5.0"),sQuery(id+"F0.wireOp",EDGE,"E5.1"),sQuery(id+"F0.wireOp",EDGE,"E5.2"),sQuery(id+"F0.wireOp",EDGE,"E5.3"),sQuery(id+"F0.wireOp",EDGE,"E5.4"),sQuery(id+"F0.wireOp",EDGE,"E5.5"),sQuery(id+"F0.wireOp",EDGE,"E6.0"),sQuery(id+"F0.wireOp",EDGE,"E6.1"),sQuery(id+"F0.wireOp",EDGE,"E6.2"),sQuery(id+"F0.wireOp",EDGE,"E6.3"),sQuery(id+"F0.wireOp",EDGE,"E6.4"),sQuery(id+"F0.wireOp",EDGE,"E6.5"),sQuery(id+"F0.wireOp",EDGE,"E7.0"),sQuery(id+"F0.wireOp",EDGE,"E7.1"),sQuery(id+"F0.wireOp",EDGE,"E7.2"),sQuery(id+"F0.wireOp",EDGE,"E7.3"),sQuery(id+"F0.wireOp",EDGE,"E7.4"),sQuery(id+"F0.wireOp",EDGE,"E7.5"),sQuery(id+"F0.wireOp",EDGE,"E8"),sQuery(id+"F0.wireOp",EDGE,"E9"),sQuery(id+"F0.wireOp",EDGE,"E10"),sQuery(id+"F0.wireOp",EDGE,"E11"),sQuery(id+"F0.wireOp",EDGE,"E13"),sQuery(id+"F0.wireOp",EDGE,"E14")])],"isStart":true}),makeQuery(id+"F4.opExtrude","SWEPT_FACE",FACE,{"disambiguationData":[OSD([sQuery(id+"F3.wireOp",EDGE,"E43.0")])]})]});
            var Q44;
            Q44=makeQuery(id+"F4.boolean.opBoolean","INTERSECT",EDGE,{"derivedFrom":[makeQuery(id+"F1.opExtrude","CAP_FACE",FACE,{"disambiguationData":[OSD([sQuery(id+"F0.wireOp",EDGE,"E0"),sQuery(id+"F0.wireOp",EDGE,"E5.0"),sQuery(id+"F0.wireOp",EDGE,"E5.1"),sQuery(id+"F0.wireOp",EDGE,"E5.2"),sQuery(id+"F0.wireOp",EDGE,"E5.3"),sQuery(id+"F0.wireOp",EDGE,"E5.4"),sQuery(id+"F0.wireOp",EDGE,"E5.5"),sQuery(id+"F0.wireOp",EDGE,"E6.0"),sQuery(id+"F0.wireOp",EDGE,"E6.1"),sQuery(id+"F0.wireOp",EDGE,"E6.2"),sQuery(id+"F0.wireOp",EDGE,"E6.3"),sQuery(id+"F0.wireOp",EDGE,"E6.4"),sQuery(id+"F0.wireOp",EDGE,"E6.5"),sQuery(id+"F0.wireOp",EDGE,"E7.0"),sQuery(id+"F0.wireOp",EDGE,"E7.1"),sQuery(id+"F0.wireOp",EDGE,"E7.2"),sQuery(id+"F0.wireOp",EDGE,"E7.3"),sQuery(id+"F0.wireOp",EDGE,"E7.4"),sQuery(id+"F0.wireOp",EDGE,"E7.5"),sQuery(id+"F0.wireOp",EDGE,"E8"),sQuery(id+"F0.wireOp",EDGE,"E9"),sQuery(id+"F0.wireOp",EDGE,"E10"),sQuery(id+"F0.wireOp",EDGE,"E11"),sQuery(id+"F0.wireOp",EDGE,"E13"),sQuery(id+"F0.wireOp",EDGE,"E14")])],"isStart":true}),makeQuery(id+"F4.opExtrude","SWEPT_FACE",FACE,{"disambiguationData":[OSD([sQuery(id+"F3.wireOp",EDGE,"E50.trimOffspring")])]})]});
            var Q45;
            Q45=makeQuery(id+"F4.boolean.opBoolean","INTERSECT",EDGE,{"derivedFrom":[makeQuery(id+"F1.opExtrude","CAP_FACE",FACE,{"disambiguationData":[OSD([sQuery(id+"F0.wireOp",EDGE,"E0"),sQuery(id+"F0.wireOp",EDGE,"E5.0"),sQuery(id+"F0.wireOp",EDGE,"E5.1"),sQuery(id+"F0.wireOp",EDGE,"E5.2"),sQuery(id+"F0.wireOp",EDGE,"E5.3"),sQuery(id+"F0.wireOp",EDGE,"E5.4"),sQuery(id+"F0.wireOp",EDGE,"E5.5"),sQuery(id+"F0.wireOp",EDGE,"E6.0"),sQuery(id+"F0.wireOp",EDGE,"E6.1"),sQuery(id+"F0.wireOp",EDGE,"E6.2"),sQuery(id+"F0.wireOp",EDGE,"E6.3"),sQuery(id+"F0.wireOp",EDGE,"E6.4"),sQuery(id+"F0.wireOp",EDGE,"E6.5"),sQuery(id+"F0.wireOp",EDGE,"E7.0"),sQuery(id+"F0.wireOp",EDGE,"E7.1"),sQuery(id+"F0.wireOp",EDGE,"E7.2"),sQuery(id+"F0.wireOp",EDGE,"E7.3"),sQuery(id+"F0.wireOp",EDGE,"E7.4"),sQuery(id+"F0.wireOp",EDGE,"E7.5"),sQuery(id+"F0.wireOp",EDGE,"E8"),sQuery(id+"F0.wireOp",EDGE,"E9"),sQuery(id+"F0.wireOp",EDGE,"E10"),sQuery(id+"F0.wireOp",EDGE,"E11"),sQuery(id+"F0.wireOp",EDGE,"E13"),sQuery(id+"F0.wireOp",EDGE,"E14")])],"isStart":true}),makeQuery(id+"F4.opExtrude","SWEPT_FACE",FACE,{"disambiguationData":[OSD([sQuery(id+"F3.wireOp",EDGE,"E21.2")])]})]});
            var Q46;
            Q46=makeQuery(id+"F4.boolean.opBoolean","INTERSECT",EDGE,{"derivedFrom":[makeQuery(id+"F1.opExtrude","CAP_FACE",FACE,{"disambiguationData":[OSD([sQuery(id+"F0.wireOp",EDGE,"E0"),sQuery(id+"F0.wireOp",EDGE,"E5.0"),sQuery(id+"F0.wireOp",EDGE,"E5.1"),sQuery(id+"F0.wireOp",EDGE,"E5.2"),sQuery(id+"F0.wireOp",EDGE,"E5.3"),sQuery(id+"F0.wireOp",EDGE,"E5.4"),sQuery(id+"F0.wireOp",EDGE,"E5.5"),sQuery(id+"F0.wireOp",EDGE,"E6.0"),sQuery(id+"F0.wireOp",EDGE,"E6.1"),sQuery(id+"F0.wireOp",EDGE,"E6.2"),sQuery(id+"F0.wireOp",EDGE,"E6.3"),sQuery(id+"F0.wireOp",EDGE,"E6.4"),sQuery(id+"F0.wireOp",EDGE,"E6.5"),sQuery(id+"F0.wireOp",EDGE,"E7.0"),sQuery(id+"F0.wireOp",EDGE,"E7.1"),sQuery(id+"F0.wireOp",EDGE,"E7.2"),sQuery(id+"F0.wireOp",EDGE,"E7.3"),sQuery(id+"F0.wireOp",EDGE,"E7.4"),sQuery(id+"F0.wireOp",EDGE,"E7.5"),sQuery(id+"F0.wireOp",EDGE,"E8"),sQuery(id+"F0.wireOp",EDGE,"E9"),sQuery(id+"F0.wireOp",EDGE,"E10"),sQuery(id+"F0.wireOp",EDGE,"E11"),sQuery(id+"F0.wireOp",EDGE,"E13"),sQuery(id+"F0.wireOp",EDGE,"E14")])],"isStart":true}),makeQuery(id+"F4.opExtrude","SWEPT_FACE",FACE,{"disambiguationData":[OSD([sQuery(id+"F3.wireOp",EDGE,"E55")])]})]});
            var Q47;
            Q47=makeQuery(id+"F4.boolean.opBoolean","INTERSECT",EDGE,{"derivedFrom":[makeQuery(id+"F1.opExtrude","CAP_FACE",FACE,{"disambiguationData":[OSD([sQuery(id+"F0.wireOp",EDGE,"E0"),sQuery(id+"F0.wireOp",EDGE,"E5.0"),sQuery(id+"F0.wireOp",EDGE,"E5.1"),sQuery(id+"F0.wireOp",EDGE,"E5.2"),sQuery(id+"F0.wireOp",EDGE,"E5.3"),sQuery(id+"F0.wireOp",EDGE,"E5.4"),sQuery(id+"F0.wireOp",EDGE,"E5.5"),sQuery(id+"F0.wireOp",EDGE,"E6.0"),sQuery(id+"F0.wireOp",EDGE,"E6.1"),sQuery(id+"F0.wireOp",EDGE,"E6.2"),sQuery(id+"F0.wireOp",EDGE,"E6.3"),sQuery(id+"F0.wireOp",EDGE,"E6.4"),sQuery(id+"F0.wireOp",EDGE,"E6.5"),sQuery(id+"F0.wireOp",EDGE,"E7.0"),sQuery(id+"F0.wireOp",EDGE,"E7.1"),sQuery(id+"F0.wireOp",EDGE,"E7.2"),sQuery(id+"F0.wireOp",EDGE,"E7.3"),sQuery(id+"F0.wireOp",EDGE,"E7.4"),sQuery(id+"F0.wireOp",EDGE,"E7.5"),sQuery(id+"F0.wireOp",EDGE,"E8"),sQuery(id+"F0.wireOp",EDGE,"E9"),sQuery(id+"F0.wireOp",EDGE,"E10"),sQuery(id+"F0.wireOp",EDGE,"E11"),sQuery(id+"F0.wireOp",EDGE,"E13"),sQuery(id+"F0.wireOp",EDGE,"E14")])],"isStart":true}),makeQuery(id+"F4.opExtrude","SWEPT_FACE",FACE,{"disambiguationData":[OSD([sQuery(id+"F3.wireOp",EDGE,"E51.trimOffspring")])]})]});
            var Q48;
            Q48=makeQuery(id+"F4.boolean.opBoolean","INTERSECT",EDGE,{"derivedFrom":[makeQuery(id+"F1.opExtrude","CAP_FACE",FACE,{"disambiguationData":[OSD([sQuery(id+"F0.wireOp",EDGE,"E0"),sQuery(id+"F0.wireOp",EDGE,"E5.0"),sQuery(id+"F0.wireOp",EDGE,"E5.1"),sQuery(id+"F0.wireOp",EDGE,"E5.2"),sQuery(id+"F0.wireOp",EDGE,"E5.3"),sQuery(id+"F0.wireOp",EDGE,"E5.4"),sQuery(id+"F0.wireOp",EDGE,"E5.5"),sQuery(id+"F0.wireOp",EDGE,"E6.0"),sQuery(id+"F0.wireOp",EDGE,"E6.1"),sQuery(id+"F0.wireOp",EDGE,"E6.2"),sQuery(id+"F0.wireOp",EDGE,"E6.3"),sQuery(id+"F0.wireOp",EDGE,"E6.4"),sQuery(id+"F0.wireOp",EDGE,"E6.5"),sQuery(id+"F0.wireOp",EDGE,"E7.0"),sQuery(id+"F0.wireOp",EDGE,"E7.1"),sQuery(id+"F0.wireOp",EDGE,"E7.2"),sQuery(id+"F0.wireOp",EDGE,"E7.3"),sQuery(id+"F0.wireOp",EDGE,"E7.4"),sQuery(id+"F0.wireOp",EDGE,"E7.5"),sQuery(id+"F0.wireOp",EDGE,"E8"),sQuery(id+"F0.wireOp",EDGE,"E9"),sQuery(id+"F0.wireOp",EDGE,"E10"),sQuery(id+"F0.wireOp",EDGE,"E11"),sQuery(id+"F0.wireOp",EDGE,"E13"),sQuery(id+"F0.wireOp",EDGE,"E14")])],"isStart":true}),makeQuery(id+"F4.opExtrude","SWEPT_FACE",FACE,{"disambiguationData":[OSD([sQuery(id+"F3.wireOp",EDGE,"E21.4")])]})]});
            var Q49;
            Q49=makeQuery(id+"F4.boolean.opBoolean","INTERSECT",EDGE,{"derivedFrom":[makeQuery(id+"F1.opExtrude","CAP_FACE",FACE,{"disambiguationData":[OSD([sQuery(id+"F0.wireOp",EDGE,"E0"),sQuery(id+"F0.wireOp",EDGE,"E5.0"),sQuery(id+"F0.wireOp",EDGE,"E5.1"),sQuery(id+"F0.wireOp",EDGE,"E5.2"),sQuery(id+"F0.wireOp",EDGE,"E5.3"),sQuery(id+"F0.wireOp",EDGE,"E5.4"),sQuery(id+"F0.wireOp",EDGE,"E5.5"),sQuery(id+"F0.wireOp",EDGE,"E6.0"),sQuery(id+"F0.wireOp",EDGE,"E6.1"),sQuery(id+"F0.wireOp",EDGE,"E6.2"),sQuery(id+"F0.wireOp",EDGE,"E6.3"),sQuery(id+"F0.wireOp",EDGE,"E6.4"),sQuery(id+"F0.wireOp",EDGE,"E6.5"),sQuery(id+"F0.wireOp",EDGE,"E7.0"),sQuery(id+"F0.wireOp",EDGE,"E7.1"),sQuery(id+"F0.wireOp",EDGE,"E7.2"),sQuery(id+"F0.wireOp",EDGE,"E7.3"),sQuery(id+"F0.wireOp",EDGE,"E7.4"),sQuery(id+"F0.wireOp",EDGE,"E7.5"),sQuery(id+"F0.wireOp",EDGE,"E8"),sQuery(id+"F0.wireOp",EDGE,"E9"),sQuery(id+"F0.wireOp",EDGE,"E10"),sQuery(id+"F0.wireOp",EDGE,"E11"),sQuery(id+"F0.wireOp",EDGE,"E13"),sQuery(id+"F0.wireOp",EDGE,"E14")])],"isStart":true}),makeQuery(id+"F4.opExtrude","SWEPT_FACE",FACE,{"disambiguationData":[OSD([sQuery(id+"F3.wireOp",EDGE,"E56")])]})]});
            var Q50;
            Q50=makeQuery(id+"F4.boolean.opBoolean","INTERSECT",EDGE,{"derivedFrom":[makeQuery(id+"F1.opExtrude","CAP_FACE",FACE,{"disambiguationData":[OSD([sQuery(id+"F0.wireOp",EDGE,"E0"),sQuery(id+"F0.wireOp",EDGE,"E5.0"),sQuery(id+"F0.wireOp",EDGE,"E5.1"),sQuery(id+"F0.wireOp",EDGE,"E5.2"),sQuery(id+"F0.wireOp",EDGE,"E5.3"),sQuery(id+"F0.wireOp",EDGE,"E5.4"),sQuery(id+"F0.wireOp",EDGE,"E5.5"),sQuery(id+"F0.wireOp",EDGE,"E6.0"),sQuery(id+"F0.wireOp",EDGE,"E6.1"),sQuery(id+"F0.wireOp",EDGE,"E6.2"),sQuery(id+"F0.wireOp",EDGE,"E6.3"),sQuery(id+"F0.wireOp",EDGE,"E6.4"),sQuery(id+"F0.wireOp",EDGE,"E6.5"),sQuery(id+"F0.wireOp",EDGE,"E7.0"),sQuery(id+"F0.wireOp",EDGE,"E7.1"),sQuery(id+"F0.wireOp",EDGE,"E7.2"),sQuery(id+"F0.wireOp",EDGE,"E7.3"),sQuery(id+"F0.wireOp",EDGE,"E7.4"),sQuery(id+"F0.wireOp",EDGE,"E7.5"),sQuery(id+"F0.wireOp",EDGE,"E8"),sQuery(id+"F0.wireOp",EDGE,"E9"),sQuery(id+"F0.wireOp",EDGE,"E10"),sQuery(id+"F0.wireOp",EDGE,"E11"),sQuery(id+"F0.wireOp",EDGE,"E13"),sQuery(id+"F0.wireOp",EDGE,"E14")])],"isStart":true}),makeQuery(id+"F4.opExtrude","SWEPT_FACE",FACE,{"disambiguationData":[OSD([sQuery(id+"F3.wireOp",EDGE,"E16.0")])]})]});
            var Q51;
            Q51=makeQuery(id+"F4.boolean.opBoolean","INTERSECT",EDGE,{"derivedFrom":[makeQuery(id+"F1.opExtrude","CAP_FACE",FACE,{"disambiguationData":[OSD([sQuery(id+"F0.wireOp",EDGE,"E0"),sQuery(id+"F0.wireOp",EDGE,"E5.0"),sQuery(id+"F0.wireOp",EDGE,"E5.1"),sQuery(id+"F0.wireOp",EDGE,"E5.2"),sQuery(id+"F0.wireOp",EDGE,"E5.3"),sQuery(id+"F0.wireOp",EDGE,"E5.4"),sQuery(id+"F0.wireOp",EDGE,"E5.5"),sQuery(id+"F0.wireOp",EDGE,"E6.0"),sQuery(id+"F0.wireOp",EDGE,"E6.1"),sQuery(id+"F0.wireOp",EDGE,"E6.2"),sQuery(id+"F0.wireOp",EDGE,"E6.3"),sQuery(id+"F0.wireOp",EDGE,"E6.4"),sQuery(id+"F0.wireOp",EDGE,"E6.5"),sQuery(id+"F0.wireOp",EDGE,"E7.0"),sQuery(id+"F0.wireOp",EDGE,"E7.1"),sQuery(id+"F0.wireOp",EDGE,"E7.2"),sQuery(id+"F0.wireOp",EDGE,"E7.3"),sQuery(id+"F0.wireOp",EDGE,"E7.4"),sQuery(id+"F0.wireOp",EDGE,"E7.5"),sQuery(id+"F0.wireOp",EDGE,"E8"),sQuery(id+"F0.wireOp",EDGE,"E9"),sQuery(id+"F0.wireOp",EDGE,"E10"),sQuery(id+"F0.wireOp",EDGE,"E11"),sQuery(id+"F0.wireOp",EDGE,"E13"),sQuery(id+"F0.wireOp",EDGE,"E14")])],"isStart":true}),makeQuery(id+"F4.opExtrude","SWEPT_FACE",FACE,{"disambiguationData":[OSD([sQuery(id+"F3.wireOp",EDGE,"E16.1")])]})]});
            var Q52;
            Q52=makeQuery(id+"F4.boolean.opBoolean","INTERSECT",EDGE,{"derivedFrom":[makeQuery(id+"F1.opExtrude","CAP_FACE",FACE,{"disambiguationData":[OSD([sQuery(id+"F0.wireOp",EDGE,"E0"),sQuery(id+"F0.wireOp",EDGE,"E5.0"),sQuery(id+"F0.wireOp",EDGE,"E5.1"),sQuery(id+"F0.wireOp",EDGE,"E5.2"),sQuery(id+"F0.wireOp",EDGE,"E5.3"),sQuery(id+"F0.wireOp",EDGE,"E5.4"),sQuery(id+"F0.wireOp",EDGE,"E5.5"),sQuery(id+"F0.wireOp",EDGE,"E6.0"),sQuery(id+"F0.wireOp",EDGE,"E6.1"),sQuery(id+"F0.wireOp",EDGE,"E6.2"),sQuery(id+"F0.wireOp",EDGE,"E6.3"),sQuery(id+"F0.wireOp",EDGE,"E6.4"),sQuery(id+"F0.wireOp",EDGE,"E6.5"),sQuery(id+"F0.wireOp",EDGE,"E7.0"),sQuery(id+"F0.wireOp",EDGE,"E7.1"),sQuery(id+"F0.wireOp",EDGE,"E7.2"),sQuery(id+"F0.wireOp",EDGE,"E7.3"),sQuery(id+"F0.wireOp",EDGE,"E7.4"),sQuery(id+"F0.wireOp",EDGE,"E7.5"),sQuery(id+"F0.wireOp",EDGE,"E8"),sQuery(id+"F0.wireOp",EDGE,"E9"),sQuery(id+"F0.wireOp",EDGE,"E10"),sQuery(id+"F0.wireOp",EDGE,"E11"),sQuery(id+"F0.wireOp",EDGE,"E13"),sQuery(id+"F0.wireOp",EDGE,"E14")])],"isStart":true}),makeQuery(id+"F4.opExtrude","SWEPT_FACE",FACE,{"disambiguationData":[OSD([sQuery(id+"F3.wireOp",EDGE,"E18.1")])]})]});
            var Q53;
            Q53=makeQuery(id+"F4.boolean.opBoolean","INTERSECT",EDGE,{"derivedFrom":[makeQuery(id+"F1.opExtrude","CAP_FACE",FACE,{"disambiguationData":[OSD([sQuery(id+"F0.wireOp",EDGE,"E0"),sQuery(id+"F0.wireOp",EDGE,"E5.0"),sQuery(id+"F0.wireOp",EDGE,"E5.1"),sQuery(id+"F0.wireOp",EDGE,"E5.2"),sQuery(id+"F0.wireOp",EDGE,"E5.3"),sQuery(id+"F0.wireOp",EDGE,"E5.4"),sQuery(id+"F0.wireOp",EDGE,"E5.5"),sQuery(id+"F0.wireOp",EDGE,"E6.0"),sQuery(id+"F0.wireOp",EDGE,"E6.1"),sQuery(id+"F0.wireOp",EDGE,"E6.2"),sQuery(id+"F0.wireOp",EDGE,"E6.3"),sQuery(id+"F0.wireOp",EDGE,"E6.4"),sQuery(id+"F0.wireOp",EDGE,"E6.5"),sQuery(id+"F0.wireOp",EDGE,"E7.0"),sQuery(id+"F0.wireOp",EDGE,"E7.1"),sQuery(id+"F0.wireOp",EDGE,"E7.2"),sQuery(id+"F0.wireOp",EDGE,"E7.3"),sQuery(id+"F0.wireOp",EDGE,"E7.4"),sQuery(id+"F0.wireOp",EDGE,"E7.5"),sQuery(id+"F0.wireOp",EDGE,"E8"),sQuery(id+"F0.wireOp",EDGE,"E9"),sQuery(id+"F0.wireOp",EDGE,"E10"),sQuery(id+"F0.wireOp",EDGE,"E11"),sQuery(id+"F0.wireOp",EDGE,"E13"),sQuery(id+"F0.wireOp",EDGE,"E14")])],"isStart":true}),makeQuery(id+"F4.opExtrude","SWEPT_FACE",FACE,{"disambiguationData":[OSD([sQuery(id+"F3.wireOp",EDGE,"E18.0")])]})]});
            var Q54;
            Q54=makeQuery(id+"F4.boolean.opBoolean","INTERSECT",EDGE,{"derivedFrom":[makeQuery(id+"F1.opExtrude","CAP_FACE",FACE,{"disambiguationData":[OSD([sQuery(id+"F0.wireOp",EDGE,"E0"),sQuery(id+"F0.wireOp",EDGE,"E5.0"),sQuery(id+"F0.wireOp",EDGE,"E5.1"),sQuery(id+"F0.wireOp",EDGE,"E5.2"),sQuery(id+"F0.wireOp",EDGE,"E5.3"),sQuery(id+"F0.wireOp",EDGE,"E5.4"),sQuery(id+"F0.wireOp",EDGE,"E5.5"),sQuery(id+"F0.wireOp",EDGE,"E6.0"),sQuery(id+"F0.wireOp",EDGE,"E6.1"),sQuery(id+"F0.wireOp",EDGE,"E6.2"),sQuery(id+"F0.wireOp",EDGE,"E6.3"),sQuery(id+"F0.wireOp",EDGE,"E6.4"),sQuery(id+"F0.wireOp",EDGE,"E6.5"),sQuery(id+"F0.wireOp",EDGE,"E7.0"),sQuery(id+"F0.wireOp",EDGE,"E7.1"),sQuery(id+"F0.wireOp",EDGE,"E7.2"),sQuery(id+"F0.wireOp",EDGE,"E7.3"),sQuery(id+"F0.wireOp",EDGE,"E7.4"),sQuery(id+"F0.wireOp",EDGE,"E7.5"),sQuery(id+"F0.wireOp",EDGE,"E8"),sQuery(id+"F0.wireOp",EDGE,"E9"),sQuery(id+"F0.wireOp",EDGE,"E10"),sQuery(id+"F0.wireOp",EDGE,"E11"),sQuery(id+"F0.wireOp",EDGE,"E13"),sQuery(id+"F0.wireOp",EDGE,"E14")])],"isStart":true}),makeQuery(id+"F4.opExtrude","SWEPT_FACE",FACE,{"disambiguationData":[OSD([sQuery(id+"F3.wireOp",EDGE,"E26.trimOffspring")])]})]});
            var Q55;
            Q55=makeQuery(id+"F4.boolean.opBoolean","INTERSECT",EDGE,{"derivedFrom":[makeQuery(id+"F1.opExtrude","CAP_FACE",FACE,{"disambiguationData":[OSD([sQuery(id+"F0.wireOp",EDGE,"E0"),sQuery(id+"F0.wireOp",EDGE,"E5.0"),sQuery(id+"F0.wireOp",EDGE,"E5.1"),sQuery(id+"F0.wireOp",EDGE,"E5.2"),sQuery(id+"F0.wireOp",EDGE,"E5.3"),sQuery(id+"F0.wireOp",EDGE,"E5.4"),sQuery(id+"F0.wireOp",EDGE,"E5.5"),sQuery(id+"F0.wireOp",EDGE,"E6.0"),sQuery(id+"F0.wireOp",EDGE,"E6.1"),sQuery(id+"F0.wireOp",EDGE,"E6.2"),sQuery(id+"F0.wireOp",EDGE,"E6.3"),sQuery(id+"F0.wireOp",EDGE,"E6.4"),sQuery(id+"F0.wireOp",EDGE,"E6.5"),sQuery(id+"F0.wireOp",EDGE,"E7.0"),sQuery(id+"F0.wireOp",EDGE,"E7.1"),sQuery(id+"F0.wireOp",EDGE,"E7.2"),sQuery(id+"F0.wireOp",EDGE,"E7.3"),sQuery(id+"F0.wireOp",EDGE,"E7.4"),sQuery(id+"F0.wireOp",EDGE,"E7.5"),sQuery(id+"F0.wireOp",EDGE,"E8"),sQuery(id+"F0.wireOp",EDGE,"E9"),sQuery(id+"F0.wireOp",EDGE,"E10"),sQuery(id+"F0.wireOp",EDGE,"E11"),sQuery(id+"F0.wireOp",EDGE,"E13"),sQuery(id+"F0.wireOp",EDGE,"E14")])],"isStart":true}),makeQuery(id+"F4.opExtrude","SWEPT_FACE",FACE,{"disambiguationData":[OSD([sQuery(id+"F3.wireOp",EDGE,"E25.trimOffspring")])]})]});
            var Q56;
            Q56=makeQuery(id+"F4.boolean.opBoolean","INTERSECT",EDGE,{"derivedFrom":[makeQuery(id+"F1.opExtrude","CAP_FACE",FACE,{"disambiguationData":[OSD([sQuery(id+"F0.wireOp",EDGE,"E0"),sQuery(id+"F0.wireOp",EDGE,"E5.0"),sQuery(id+"F0.wireOp",EDGE,"E5.1"),sQuery(id+"F0.wireOp",EDGE,"E5.2"),sQuery(id+"F0.wireOp",EDGE,"E5.3"),sQuery(id+"F0.wireOp",EDGE,"E5.4"),sQuery(id+"F0.wireOp",EDGE,"E5.5"),sQuery(id+"F0.wireOp",EDGE,"E6.0"),sQuery(id+"F0.wireOp",EDGE,"E6.1"),sQuery(id+"F0.wireOp",EDGE,"E6.2"),sQuery(id+"F0.wireOp",EDGE,"E6.3"),sQuery(id+"F0.wireOp",EDGE,"E6.4"),sQuery(id+"F0.wireOp",EDGE,"E6.5"),sQuery(id+"F0.wireOp",EDGE,"E7.0"),sQuery(id+"F0.wireOp",EDGE,"E7.1"),sQuery(id+"F0.wireOp",EDGE,"E7.2"),sQuery(id+"F0.wireOp",EDGE,"E7.3"),sQuery(id+"F0.wireOp",EDGE,"E7.4"),sQuery(id+"F0.wireOp",EDGE,"E7.5"),sQuery(id+"F0.wireOp",EDGE,"E8"),sQuery(id+"F0.wireOp",EDGE,"E9"),sQuery(id+"F0.wireOp",EDGE,"E10"),sQuery(id+"F0.wireOp",EDGE,"E11"),sQuery(id+"F0.wireOp",EDGE,"E13"),sQuery(id+"F0.wireOp",EDGE,"E14")])],"isStart":true}),makeQuery(id+"F4.opExtrude","SWEPT_FACE",FACE,{"disambiguationData":[OSD([sQuery(id+"F3.wireOp",EDGE,"E21.1")])]})]});
            var Q57;
            Q57=makeQuery(id+"F4.boolean.opBoolean","INTERSECT",EDGE,{"derivedFrom":[makeQuery(id+"F1.opExtrude","CAP_FACE",FACE,{"disambiguationData":[OSD([sQuery(id+"F0.wireOp",EDGE,"E0"),sQuery(id+"F0.wireOp",EDGE,"E5.0"),sQuery(id+"F0.wireOp",EDGE,"E5.1"),sQuery(id+"F0.wireOp",EDGE,"E5.2"),sQuery(id+"F0.wireOp",EDGE,"E5.3"),sQuery(id+"F0.wireOp",EDGE,"E5.4"),sQuery(id+"F0.wireOp",EDGE,"E5.5"),sQuery(id+"F0.wireOp",EDGE,"E6.0"),sQuery(id+"F0.wireOp",EDGE,"E6.1"),sQuery(id+"F0.wireOp",EDGE,"E6.2"),sQuery(id+"F0.wireOp",EDGE,"E6.3"),sQuery(id+"F0.wireOp",EDGE,"E6.4"),sQuery(id+"F0.wireOp",EDGE,"E6.5"),sQuery(id+"F0.wireOp",EDGE,"E7.0"),sQuery(id+"F0.wireOp",EDGE,"E7.1"),sQuery(id+"F0.wireOp",EDGE,"E7.2"),sQuery(id+"F0.wireOp",EDGE,"E7.3"),sQuery(id+"F0.wireOp",EDGE,"E7.4"),sQuery(id+"F0.wireOp",EDGE,"E7.5"),sQuery(id+"F0.wireOp",EDGE,"E8"),sQuery(id+"F0.wireOp",EDGE,"E9"),sQuery(id+"F0.wireOp",EDGE,"E10"),sQuery(id+"F0.wireOp",EDGE,"E11"),sQuery(id+"F0.wireOp",EDGE,"E13"),sQuery(id+"F0.wireOp",EDGE,"E14")])],"isStart":true}),makeQuery(id+"F4.opExtrude","SWEPT_FACE",FACE,{"disambiguationData":[OSD([sQuery(id+"F3.wireOp",EDGE,"E21.3")])]})]});
            var Q58;
            Q58=makeQuery(id+"F4.boolean.opBoolean","INTERSECT",EDGE,{"derivedFrom":[makeQuery(id+"F1.opExtrude","CAP_FACE",FACE,{"disambiguationData":[OSD([sQuery(id+"F0.wireOp",EDGE,"E0"),sQuery(id+"F0.wireOp",EDGE,"E5.0"),sQuery(id+"F0.wireOp",EDGE,"E5.1"),sQuery(id+"F0.wireOp",EDGE,"E5.2"),sQuery(id+"F0.wireOp",EDGE,"E5.3"),sQuery(id+"F0.wireOp",EDGE,"E5.4"),sQuery(id+"F0.wireOp",EDGE,"E5.5"),sQuery(id+"F0.wireOp",EDGE,"E6.0"),sQuery(id+"F0.wireOp",EDGE,"E6.1"),sQuery(id+"F0.wireOp",EDGE,"E6.2"),sQuery(id+"F0.wireOp",EDGE,"E6.3"),sQuery(id+"F0.wireOp",EDGE,"E6.4"),sQuery(id+"F0.wireOp",EDGE,"E6.5"),sQuery(id+"F0.wireOp",EDGE,"E7.0"),sQuery(id+"F0.wireOp",EDGE,"E7.1"),sQuery(id+"F0.wireOp",EDGE,"E7.2"),sQuery(id+"F0.wireOp",EDGE,"E7.3"),sQuery(id+"F0.wireOp",EDGE,"E7.4"),sQuery(id+"F0.wireOp",EDGE,"E7.5"),sQuery(id+"F0.wireOp",EDGE,"E8"),sQuery(id+"F0.wireOp",EDGE,"E9"),sQuery(id+"F0.wireOp",EDGE,"E10"),sQuery(id+"F0.wireOp",EDGE,"E11"),sQuery(id+"F0.wireOp",EDGE,"E13"),sQuery(id+"F0.wireOp",EDGE,"E14")])],"isStart":true}),makeQuery(id+"F4.opExtrude","SWEPT_FACE",FACE,{"disambiguationData":[OSD([sQuery(id+"F3.wireOp",EDGE,"E54")])]})]});
            var Q59;
            Q59=makeQuery(id+"F4.boolean.opBoolean","INTERSECT",EDGE,{"derivedFrom":[makeQuery(id+"F1.opExtrude","CAP_FACE",FACE,{"disambiguationData":[OSD([sQuery(id+"F0.wireOp",EDGE,"E0"),sQuery(id+"F0.wireOp",EDGE,"E5.0"),sQuery(id+"F0.wireOp",EDGE,"E5.1"),sQuery(id+"F0.wireOp",EDGE,"E5.2"),sQuery(id+"F0.wireOp",EDGE,"E5.3"),sQuery(id+"F0.wireOp",EDGE,"E5.4"),sQuery(id+"F0.wireOp",EDGE,"E5.5"),sQuery(id+"F0.wireOp",EDGE,"E6.0"),sQuery(id+"F0.wireOp",EDGE,"E6.1"),sQuery(id+"F0.wireOp",EDGE,"E6.2"),sQuery(id+"F0.wireOp",EDGE,"E6.3"),sQuery(id+"F0.wireOp",EDGE,"E6.4"),sQuery(id+"F0.wireOp",EDGE,"E6.5"),sQuery(id+"F0.wireOp",EDGE,"E7.0"),sQuery(id+"F0.wireOp",EDGE,"E7.1"),sQuery(id+"F0.wireOp",EDGE,"E7.2"),sQuery(id+"F0.wireOp",EDGE,"E7.3"),sQuery(id+"F0.wireOp",EDGE,"E7.4"),sQuery(id+"F0.wireOp",EDGE,"E7.5"),sQuery(id+"F0.wireOp",EDGE,"E8"),sQuery(id+"F0.wireOp",EDGE,"E9"),sQuery(id+"F0.wireOp",EDGE,"E10"),sQuery(id+"F0.wireOp",EDGE,"E11"),sQuery(id+"F0.wireOp",EDGE,"E13"),sQuery(id+"F0.wireOp",EDGE,"E14")])],"isStart":true}),makeQuery(id+"F4.opExtrude","SWEPT_FACE",FACE,{"disambiguationData":[OSD([sQuery(id+"F3.wireOp",EDGE,"E58.trimOffspring")])]})]});
            fillet(context, id + "F5", {"entities" : qUnion([Q0, Q1, Q2, Q3, Q4, Q5, Q6, Q7, Q8, Q9, Q10, Q11, Q12, Q13, Q14, Q15, Q16, Q17, Q18, Q19, Q20, Q21, Q22, Q23, Q24, Q25, Q26, Q27, Q28, Q29, Q30, Q31, Q32, Q33, Q34, Q35, Q36, Q37, Q38, Q39, Q40, Q41, Q42, Q43, Q44, Q45, Q46, Q47, Q48, Q49, Q50, Q51, Q52, Q53, Q54, Q55, Q56, Q57, Q58, Q59]), "radius" : 2 * mm, "tangentPropagation" : true, "allowEdgeOverflow" : false});
        }
        {
            var Q0;
            Q0=makeQuery(id+"F1.opExtrude","CAP_EDGE",EDGE,{"disambiguationData":[OSD([sQuery(id+"F0.wireOp",EDGE,"E0")])],"isStart":false});
            var Q1;
            Q1=makeQuery(id+"F4.boolean.opBoolean","COPY",EDGE,{"derivedFrom":makeQuery(id+"F4.opExtrude","CAP_EDGE",EDGE,{"disambiguationData":[OSD([sQuery(id+"F3.wireOp",EDGE,"E19.1")])],"isStart":true})});
            var Q2;
            Q2=makeQuery(id+"F4.boolean.opBoolean","COPY",EDGE,{"derivedFrom":makeQuery(id+"F4.opExtrude","CAP_EDGE",EDGE,{"disambiguationData":[OSD([sQuery(id+"F3.wireOp",EDGE,"E19.0")])],"isStart":true})});
            var Q3;
            Q3=makeQuery(id+"F4.boolean.opBoolean","COPY",EDGE,{"derivedFrom":makeQuery(id+"F4.opExtrude","CAP_EDGE",EDGE,{"disambiguationData":[OSD([sQuery(id+"F3.wireOp",EDGE,"E32.1")])],"isStart":true})});
            var Q4;
            Q4=makeQuery(id+"F4.boolean.opBoolean","COPY",EDGE,{"derivedFrom":makeQuery(id+"F4.opExtrude","CAP_EDGE",EDGE,{"disambiguationData":[OSD([sQuery(id+"F3.wireOp",EDGE,"E32.0")])],"isStart":true})});
            var Q5;
            Q5=makeQuery(id+"F4.boolean.opBoolean","COPY",EDGE,{"derivedFrom":makeQuery(id+"F4.opExtrude","CAP_EDGE",EDGE,{"disambiguationData":[OSD([sQuery(id+"F3.wireOp",EDGE,"E44.1")])],"isStart":true})});
            var Q6;
            Q6=makeQuery(id+"F4.boolean.opBoolean","COPY",EDGE,{"derivedFrom":makeQuery(id+"F4.opExtrude","CAP_EDGE",EDGE,{"disambiguationData":[OSD([sQuery(id+"F3.wireOp",EDGE,"E44.0")])],"isStart":true})});
            var Q7;
            Q7=makeQuery(id+"F4.boolean.opBoolean","COPY",EDGE,{"derivedFrom":makeQuery(id+"F4.opExtrude","CAP_EDGE",EDGE,{"disambiguationData":[OSD([sQuery(id+"F3.wireOp",EDGE,"E52.trimOffspring")])],"isStart":true})});
            var Q8;
            Q8=makeQuery(id+"F4.boolean.opBoolean","COPY",EDGE,{"derivedFrom":makeQuery(id+"F4.opExtrude","CAP_EDGE",EDGE,{"disambiguationData":[OSD([sQuery(id+"F3.wireOp",EDGE,"E20.3")])],"isStart":true})});
            var Q9;
            Q9=makeQuery(id+"F4.boolean.opBoolean","COPY",EDGE,{"derivedFrom":makeQuery(id+"F4.opExtrude","CAP_EDGE",EDGE,{"disambiguationData":[OSD([sQuery(id+"F3.wireOp",EDGE,"E20.4")])],"isStart":true})});
            var Q10;
            Q10=makeQuery(id+"F4.boolean.opBoolean","COPY",EDGE,{"derivedFrom":makeQuery(id+"F4.opExtrude","CAP_EDGE",EDGE,{"disambiguationData":[OSD([sQuery(id+"F3.wireOp",EDGE,"E20.5")])],"isStart":true})});
            var Q11;
            Q11=makeQuery(id+"F4.boolean.opBoolean","COPY",EDGE,{"derivedFrom":makeQuery(id+"F4.opExtrude","CAP_EDGE",EDGE,{"disambiguationData":[OSD([sQuery(id+"F3.wireOp",EDGE,"E20.0")])],"isStart":true})});
            var Q12;
            Q12=makeQuery(id+"F4.boolean.opBoolean","COPY",EDGE,{"derivedFrom":makeQuery(id+"F4.opExtrude","CAP_EDGE",EDGE,{"disambiguationData":[OSD([sQuery(id+"F3.wireOp",EDGE,"E20.1")])],"isStart":true})});
            var Q13;
            Q13=makeQuery(id+"F4.boolean.opBoolean","INTERSECT",EDGE,{"derivedFrom":[makeQuery(id+"F1.opExtrude","CAP_FACE",FACE,{"disambiguationData":[OSD([sQuery(id+"F0.wireOp",EDGE,"E0"),sQuery(id+"F0.wireOp",EDGE,"E5.0"),sQuery(id+"F0.wireOp",EDGE,"E5.1"),sQuery(id+"F0.wireOp",EDGE,"E5.2"),sQuery(id+"F0.wireOp",EDGE,"E5.3"),sQuery(id+"F0.wireOp",EDGE,"E5.4"),sQuery(id+"F0.wireOp",EDGE,"E5.5"),sQuery(id+"F0.wireOp",EDGE,"E6.0"),sQuery(id+"F0.wireOp",EDGE,"E6.1"),sQuery(id+"F0.wireOp",EDGE,"E6.2"),sQuery(id+"F0.wireOp",EDGE,"E6.3"),sQuery(id+"F0.wireOp",EDGE,"E6.4"),sQuery(id+"F0.wireOp",EDGE,"E6.5"),sQuery(id+"F0.wireOp",EDGE,"E7.0"),sQuery(id+"F0.wireOp",EDGE,"E7.1"),sQuery(id+"F0.wireOp",EDGE,"E7.2"),sQuery(id+"F0.wireOp",EDGE,"E7.3"),sQuery(id+"F0.wireOp",EDGE,"E7.4"),sQuery(id+"F0.wireOp",EDGE,"E7.5"),sQuery(id+"F0.wireOp",EDGE,"E8"),sQuery(id+"F0.wireOp",EDGE,"E9"),sQuery(id+"F0.wireOp",EDGE,"E10"),sQuery(id+"F0.wireOp",EDGE,"E11"),sQuery(id+"F0.wireOp",EDGE,"E13"),sQuery(id+"F0.wireOp",EDGE,"E14")])],"isStart":true}),makeQuery(id+"F4.opExtrude","SWEPT_FACE",FACE,{"disambiguationData":[OSD([sQuery(id+"F3.wireOp",EDGE,"E32.0")])]})]});
            var Q14;
            Q14=makeQuery(id+"F4.boolean.opBoolean","INTERSECT",EDGE,{"derivedFrom":[makeQuery(id+"F1.opExtrude","CAP_FACE",FACE,{"disambiguationData":[OSD([sQuery(id+"F0.wireOp",EDGE,"E0"),sQuery(id+"F0.wireOp",EDGE,"E5.0"),sQuery(id+"F0.wireOp",EDGE,"E5.1"),sQuery(id+"F0.wireOp",EDGE,"E5.2"),sQuery(id+"F0.wireOp",EDGE,"E5.3"),sQuery(id+"F0.wireOp",EDGE,"E5.4"),sQuery(id+"F0.wireOp",EDGE,"E5.5"),sQuery(id+"F0.wireOp",EDGE,"E6.0"),sQuery(id+"F0.wireOp",EDGE,"E6.1"),sQuery(id+"F0.wireOp",EDGE,"E6.2"),sQuery(id+"F0.wireOp",EDGE,"E6.3"),sQuery(id+"F0.wireOp",EDGE,"E6.4"),sQuery(id+"F0.wireOp",EDGE,"E6.5"),sQuery(id+"F0.wireOp",EDGE,"E7.0"),sQuery(id+"F0.wireOp",EDGE,"E7.1"),sQuery(id+"F0.wireOp",EDGE,"E7.2"),sQuery(id+"F0.wireOp",EDGE,"E7.3"),sQuery(id+"F0.wireOp",EDGE,"E7.4"),sQuery(id+"F0.wireOp",EDGE,"E7.5"),sQuery(id+"F0.wireOp",EDGE,"E8"),sQuery(id+"F0.wireOp",EDGE,"E9"),sQuery(id+"F0.wireOp",EDGE,"E10"),sQuery(id+"F0.wireOp",EDGE,"E11"),sQuery(id+"F0.wireOp",EDGE,"E13"),sQuery(id+"F0.wireOp",EDGE,"E14")])],"isStart":true}),makeQuery(id+"F4.opExtrude","SWEPT_FACE",FACE,{"disambiguationData":[OSD([sQuery(id+"F3.wireOp",EDGE,"E32.1")])]})]});
            var Q15;
            Q15=makeQuery(id+"F4.boolean.opBoolean","INTERSECT",EDGE,{"derivedFrom":[makeQuery(id+"F1.opExtrude","CAP_FACE",FACE,{"disambiguationData":[OSD([sQuery(id+"F0.wireOp",EDGE,"E0"),sQuery(id+"F0.wireOp",EDGE,"E5.0"),sQuery(id+"F0.wireOp",EDGE,"E5.1"),sQuery(id+"F0.wireOp",EDGE,"E5.2"),sQuery(id+"F0.wireOp",EDGE,"E5.3"),sQuery(id+"F0.wireOp",EDGE,"E5.4"),sQuery(id+"F0.wireOp",EDGE,"E5.5"),sQuery(id+"F0.wireOp",EDGE,"E6.0"),sQuery(id+"F0.wireOp",EDGE,"E6.1"),sQuery(id+"F0.wireOp",EDGE,"E6.2"),sQuery(id+"F0.wireOp",EDGE,"E6.3"),sQuery(id+"F0.wireOp",EDGE,"E6.4"),sQuery(id+"F0.wireOp",EDGE,"E6.5"),sQuery(id+"F0.wireOp",EDGE,"E7.0"),sQuery(id+"F0.wireOp",EDGE,"E7.1"),sQuery(id+"F0.wireOp",EDGE,"E7.2"),sQuery(id+"F0.wireOp",EDGE,"E7.3"),sQuery(id+"F0.wireOp",EDGE,"E7.4"),sQuery(id+"F0.wireOp",EDGE,"E7.5"),sQuery(id+"F0.wireOp",EDGE,"E8"),sQuery(id+"F0.wireOp",EDGE,"E9"),sQuery(id+"F0.wireOp",EDGE,"E10"),sQuery(id+"F0.wireOp",EDGE,"E11"),sQuery(id+"F0.wireOp",EDGE,"E13"),sQuery(id+"F0.wireOp",EDGE,"E14")])],"isStart":true}),makeQuery(id+"F4.opExtrude","SWEPT_FACE",FACE,{"disambiguationData":[OSD([sQuery(id+"F3.wireOp",EDGE,"E44.1")])]})]});
            var Q16;
            Q16=makeQuery(id+"F4.boolean.opBoolean","INTERSECT",EDGE,{"derivedFrom":[makeQuery(id+"F1.opExtrude","CAP_FACE",FACE,{"disambiguationData":[OSD([sQuery(id+"F0.wireOp",EDGE,"E0"),sQuery(id+"F0.wireOp",EDGE,"E5.0"),sQuery(id+"F0.wireOp",EDGE,"E5.1"),sQuery(id+"F0.wireOp",EDGE,"E5.2"),sQuery(id+"F0.wireOp",EDGE,"E5.3"),sQuery(id+"F0.wireOp",EDGE,"E5.4"),sQuery(id+"F0.wireOp",EDGE,"E5.5"),sQuery(id+"F0.wireOp",EDGE,"E6.0"),sQuery(id+"F0.wireOp",EDGE,"E6.1"),sQuery(id+"F0.wireOp",EDGE,"E6.2"),sQuery(id+"F0.wireOp",EDGE,"E6.3"),sQuery(id+"F0.wireOp",EDGE,"E6.4"),sQuery(id+"F0.wireOp",EDGE,"E6.5"),sQuery(id+"F0.wireOp",EDGE,"E7.0"),sQuery(id+"F0.wireOp",EDGE,"E7.1"),sQuery(id+"F0.wireOp",EDGE,"E7.2"),sQuery(id+"F0.wireOp",EDGE,"E7.3"),sQuery(id+"F0.wireOp",EDGE,"E7.4"),sQuery(id+"F0.wireOp",EDGE,"E7.5"),sQuery(id+"F0.wireOp",EDGE,"E8"),sQuery(id+"F0.wireOp",EDGE,"E9"),sQuery(id+"F0.wireOp",EDGE,"E10"),sQuery(id+"F0.wireOp",EDGE,"E11"),sQuery(id+"F0.wireOp",EDGE,"E13"),sQuery(id+"F0.wireOp",EDGE,"E14")])],"isStart":true}),makeQuery(id+"F4.opExtrude","SWEPT_FACE",FACE,{"disambiguationData":[OSD([sQuery(id+"F3.wireOp",EDGE,"E44.0")])]})]});
            var Q17;
            Q17=makeQuery(id+"F4.boolean.opBoolean","INTERSECT",EDGE,{"derivedFrom":[makeQuery(id+"F1.opExtrude","CAP_FACE",FACE,{"disambiguationData":[OSD([sQuery(id+"F0.wireOp",EDGE,"E0"),sQuery(id+"F0.wireOp",EDGE,"E5.0"),sQuery(id+"F0.wireOp",EDGE,"E5.1"),sQuery(id+"F0.wireOp",EDGE,"E5.2"),sQuery(id+"F0.wireOp",EDGE,"E5.3"),sQuery(id+"F0.wireOp",EDGE,"E5.4"),sQuery(id+"F0.wireOp",EDGE,"E5.5"),sQuery(id+"F0.wireOp",EDGE,"E6.0"),sQuery(id+"F0.wireOp",EDGE,"E6.1"),sQuery(id+"F0.wireOp",EDGE,"E6.2"),sQuery(id+"F0.wireOp",EDGE,"E6.3"),sQuery(id+"F0.wireOp",EDGE,"E6.4"),sQuery(id+"F0.wireOp",EDGE,"E6.5"),sQuery(id+"F0.wireOp",EDGE,"E7.0"),sQuery(id+"F0.wireOp",EDGE,"E7.1"),sQuery(id+"F0.wireOp",EDGE,"E7.2"),sQuery(id+"F0.wireOp",EDGE,"E7.3"),sQuery(id+"F0.wireOp",EDGE,"E7.4"),sQuery(id+"F0.wireOp",EDGE,"E7.5"),sQuery(id+"F0.wireOp",EDGE,"E8"),sQuery(id+"F0.wireOp",EDGE,"E9"),sQuery(id+"F0.wireOp",EDGE,"E10"),sQuery(id+"F0.wireOp",EDGE,"E11"),sQuery(id+"F0.wireOp",EDGE,"E13"),sQuery(id+"F0.wireOp",EDGE,"E14")])],"isStart":true}),makeQuery(id+"F4.opExtrude","SWEPT_FACE",FACE,{"disambiguationData":[OSD([sQuery(id+"F3.wireOp",EDGE,"E19.1")])]})]});
            var Q18;
            Q18=makeQuery(id+"F4.boolean.opBoolean","INTERSECT",EDGE,{"derivedFrom":[makeQuery(id+"F1.opExtrude","CAP_FACE",FACE,{"disambiguationData":[OSD([sQuery(id+"F0.wireOp",EDGE,"E0"),sQuery(id+"F0.wireOp",EDGE,"E5.0"),sQuery(id+"F0.wireOp",EDGE,"E5.1"),sQuery(id+"F0.wireOp",EDGE,"E5.2"),sQuery(id+"F0.wireOp",EDGE,"E5.3"),sQuery(id+"F0.wireOp",EDGE,"E5.4"),sQuery(id+"F0.wireOp",EDGE,"E5.5"),sQuery(id+"F0.wireOp",EDGE,"E6.0"),sQuery(id+"F0.wireOp",EDGE,"E6.1"),sQuery(id+"F0.wireOp",EDGE,"E6.2"),sQuery(id+"F0.wireOp",EDGE,"E6.3"),sQuery(id+"F0.wireOp",EDGE,"E6.4"),sQuery(id+"F0.wireOp",EDGE,"E6.5"),sQuery(id+"F0.wireOp",EDGE,"E7.0"),sQuery(id+"F0.wireOp",EDGE,"E7.1"),sQuery(id+"F0.wireOp",EDGE,"E7.2"),sQuery(id+"F0.wireOp",EDGE,"E7.3"),sQuery(id+"F0.wireOp",EDGE,"E7.4"),sQuery(id+"F0.wireOp",EDGE,"E7.5"),sQuery(id+"F0.wireOp",EDGE,"E8"),sQuery(id+"F0.wireOp",EDGE,"E9"),sQuery(id+"F0.wireOp",EDGE,"E10"),sQuery(id+"F0.wireOp",EDGE,"E11"),sQuery(id+"F0.wireOp",EDGE,"E13"),sQuery(id+"F0.wireOp",EDGE,"E14")])],"isStart":true}),makeQuery(id+"F4.opExtrude","SWEPT_FACE",FACE,{"disambiguationData":[OSD([sQuery(id+"F3.wireOp",EDGE,"E19.0")])]})]});
            var Q19;
            Q19=makeQuery(id+"F4.boolean.opBoolean","INTERSECT",EDGE,{"derivedFrom":[makeQuery(id+"F1.opExtrude","CAP_FACE",FACE,{"disambiguationData":[OSD([sQuery(id+"F0.wireOp",EDGE,"E0"),sQuery(id+"F0.wireOp",EDGE,"E5.0"),sQuery(id+"F0.wireOp",EDGE,"E5.1"),sQuery(id+"F0.wireOp",EDGE,"E5.2"),sQuery(id+"F0.wireOp",EDGE,"E5.3"),sQuery(id+"F0.wireOp",EDGE,"E5.4"),sQuery(id+"F0.wireOp",EDGE,"E5.5"),sQuery(id+"F0.wireOp",EDGE,"E6.0"),sQuery(id+"F0.wireOp",EDGE,"E6.1"),sQuery(id+"F0.wireOp",EDGE,"E6.2"),sQuery(id+"F0.wireOp",EDGE,"E6.3"),sQuery(id+"F0.wireOp",EDGE,"E6.4"),sQuery(id+"F0.wireOp",EDGE,"E6.5"),sQuery(id+"F0.wireOp",EDGE,"E7.0"),sQuery(id+"F0.wireOp",EDGE,"E7.1"),sQuery(id+"F0.wireOp",EDGE,"E7.2"),sQuery(id+"F0.wireOp",EDGE,"E7.3"),sQuery(id+"F0.wireOp",EDGE,"E7.4"),sQuery(id+"F0.wireOp",EDGE,"E7.5"),sQuery(id+"F0.wireOp",EDGE,"E8"),sQuery(id+"F0.wireOp",EDGE,"E9"),sQuery(id+"F0.wireOp",EDGE,"E10"),sQuery(id+"F0.wireOp",EDGE,"E11"),sQuery(id+"F0.wireOp",EDGE,"E13"),sQuery(id+"F0.wireOp",EDGE,"E14")])],"isStart":true}),makeQuery(id+"F4.opExtrude","SWEPT_FACE",FACE,{"disambiguationData":[OSD([sQuery(id+"F3.wireOp",EDGE,"E20.5")])]})]});
            var Q20;
            Q20=makeQuery(id+"F4.boolean.opBoolean","INTERSECT",EDGE,{"derivedFrom":[makeQuery(id+"F1.opExtrude","CAP_FACE",FACE,{"disambiguationData":[OSD([sQuery(id+"F0.wireOp",EDGE,"E0"),sQuery(id+"F0.wireOp",EDGE,"E5.0"),sQuery(id+"F0.wireOp",EDGE,"E5.1"),sQuery(id+"F0.wireOp",EDGE,"E5.2"),sQuery(id+"F0.wireOp",EDGE,"E5.3"),sQuery(id+"F0.wireOp",EDGE,"E5.4"),sQuery(id+"F0.wireOp",EDGE,"E5.5"),sQuery(id+"F0.wireOp",EDGE,"E6.0"),sQuery(id+"F0.wireOp",EDGE,"E6.1"),sQuery(id+"F0.wireOp",EDGE,"E6.2"),sQuery(id+"F0.wireOp",EDGE,"E6.3"),sQuery(id+"F0.wireOp",EDGE,"E6.4"),sQuery(id+"F0.wireOp",EDGE,"E6.5"),sQuery(id+"F0.wireOp",EDGE,"E7.0"),sQuery(id+"F0.wireOp",EDGE,"E7.1"),sQuery(id+"F0.wireOp",EDGE,"E7.2"),sQuery(id+"F0.wireOp",EDGE,"E7.3"),sQuery(id+"F0.wireOp",EDGE,"E7.4"),sQuery(id+"F0.wireOp",EDGE,"E7.5"),sQuery(id+"F0.wireOp",EDGE,"E8"),sQuery(id+"F0.wireOp",EDGE,"E9"),sQuery(id+"F0.wireOp",EDGE,"E10"),sQuery(id+"F0.wireOp",EDGE,"E11"),sQuery(id+"F0.wireOp",EDGE,"E13"),sQuery(id+"F0.wireOp",EDGE,"E14")])],"isStart":true}),makeQuery(id+"F4.opExtrude","SWEPT_FACE",FACE,{"disambiguationData":[OSD([sQuery(id+"F3.wireOp",EDGE,"E20.4")])]})]});
            var Q21;
            Q21=makeQuery(id+"F4.boolean.opBoolean","INTERSECT",EDGE,{"derivedFrom":[makeQuery(id+"F1.opExtrude","CAP_FACE",FACE,{"disambiguationData":[OSD([sQuery(id+"F0.wireOp",EDGE,"E0"),sQuery(id+"F0.wireOp",EDGE,"E5.0"),sQuery(id+"F0.wireOp",EDGE,"E5.1"),sQuery(id+"F0.wireOp",EDGE,"E5.2"),sQuery(id+"F0.wireOp",EDGE,"E5.3"),sQuery(id+"F0.wireOp",EDGE,"E5.4"),sQuery(id+"F0.wireOp",EDGE,"E5.5"),sQuery(id+"F0.wireOp",EDGE,"E6.0"),sQuery(id+"F0.wireOp",EDGE,"E6.1"),sQuery(id+"F0.wireOp",EDGE,"E6.2"),sQuery(id+"F0.wireOp",EDGE,"E6.3"),sQuery(id+"F0.wireOp",EDGE,"E6.4"),sQuery(id+"F0.wireOp",EDGE,"E6.5"),sQuery(id+"F0.wireOp",EDGE,"E7.0"),sQuery(id+"F0.wireOp",EDGE,"E7.1"),sQuery(id+"F0.wireOp",EDGE,"E7.2"),sQuery(id+"F0.wireOp",EDGE,"E7.3"),sQuery(id+"F0.wireOp",EDGE,"E7.4"),sQuery(id+"F0.wireOp",EDGE,"E7.5"),sQuery(id+"F0.wireOp",EDGE,"E8"),sQuery(id+"F0.wireOp",EDGE,"E9"),sQuery(id+"F0.wireOp",EDGE,"E10"),sQuery(id+"F0.wireOp",EDGE,"E11"),sQuery(id+"F0.wireOp",EDGE,"E13"),sQuery(id+"F0.wireOp",EDGE,"E14")])],"isStart":true}),makeQuery(id+"F4.opExtrude","SWEPT_FACE",FACE,{"disambiguationData":[OSD([sQuery(id+"F3.wireOp",EDGE,"E20.3")])]})]});
            var Q22;
            Q22=makeQuery(id+"F4.boolean.opBoolean","INTERSECT",EDGE,{"derivedFrom":[makeQuery(id+"F1.opExtrude","CAP_FACE",FACE,{"disambiguationData":[OSD([sQuery(id+"F0.wireOp",EDGE,"E0"),sQuery(id+"F0.wireOp",EDGE,"E5.0"),sQuery(id+"F0.wireOp",EDGE,"E5.1"),sQuery(id+"F0.wireOp",EDGE,"E5.2"),sQuery(id+"F0.wireOp",EDGE,"E5.3"),sQuery(id+"F0.wireOp",EDGE,"E5.4"),sQuery(id+"F0.wireOp",EDGE,"E5.5"),sQuery(id+"F0.wireOp",EDGE,"E6.0"),sQuery(id+"F0.wireOp",EDGE,"E6.1"),sQuery(id+"F0.wireOp",EDGE,"E6.2"),sQuery(id+"F0.wireOp",EDGE,"E6.3"),sQuery(id+"F0.wireOp",EDGE,"E6.4"),sQuery(id+"F0.wireOp",EDGE,"E6.5"),sQuery(id+"F0.wireOp",EDGE,"E7.0"),sQuery(id+"F0.wireOp",EDGE,"E7.1"),sQuery(id+"F0.wireOp",EDGE,"E7.2"),sQuery(id+"F0.wireOp",EDGE,"E7.3"),sQuery(id+"F0.wireOp",EDGE,"E7.4"),sQuery(id+"F0.wireOp",EDGE,"E7.5"),sQuery(id+"F0.wireOp",EDGE,"E8"),sQuery(id+"F0.wireOp",EDGE,"E9"),sQuery(id+"F0.wireOp",EDGE,"E10"),sQuery(id+"F0.wireOp",EDGE,"E11"),sQuery(id+"F0.wireOp",EDGE,"E13"),sQuery(id+"F0.wireOp",EDGE,"E14")])],"isStart":true}),makeQuery(id+"F4.opExtrude","SWEPT_FACE",FACE,{"disambiguationData":[OSD([sQuery(id+"F3.wireOp",EDGE,"E52.trimOffspring")])]})]});
            var Q23;
            Q23=makeQuery(id+"F4.boolean.opBoolean","INTERSECT",EDGE,{"derivedFrom":[makeQuery(id+"F1.opExtrude","CAP_FACE",FACE,{"disambiguationData":[OSD([sQuery(id+"F0.wireOp",EDGE,"E0"),sQuery(id+"F0.wireOp",EDGE,"E5.0"),sQuery(id+"F0.wireOp",EDGE,"E5.1"),sQuery(id+"F0.wireOp",EDGE,"E5.2"),sQuery(id+"F0.wireOp",EDGE,"E5.3"),sQuery(id+"F0.wireOp",EDGE,"E5.4"),sQuery(id+"F0.wireOp",EDGE,"E5.5"),sQuery(id+"F0.wireOp",EDGE,"E6.0"),sQuery(id+"F0.wireOp",EDGE,"E6.1"),sQuery(id+"F0.wireOp",EDGE,"E6.2"),sQuery(id+"F0.wireOp",EDGE,"E6.3"),sQuery(id+"F0.wireOp",EDGE,"E6.4"),sQuery(id+"F0.wireOp",EDGE,"E6.5"),sQuery(id+"F0.wireOp",EDGE,"E7.0"),sQuery(id+"F0.wireOp",EDGE,"E7.1"),sQuery(id+"F0.wireOp",EDGE,"E7.2"),sQuery(id+"F0.wireOp",EDGE,"E7.3"),sQuery(id+"F0.wireOp",EDGE,"E7.4"),sQuery(id+"F0.wireOp",EDGE,"E7.5"),sQuery(id+"F0.wireOp",EDGE,"E8"),sQuery(id+"F0.wireOp",EDGE,"E9"),sQuery(id+"F0.wireOp",EDGE,"E10"),sQuery(id+"F0.wireOp",EDGE,"E11"),sQuery(id+"F0.wireOp",EDGE,"E13"),sQuery(id+"F0.wireOp",EDGE,"E14")])],"isStart":true}),makeQuery(id+"F4.opExtrude","SWEPT_FACE",FACE,{"disambiguationData":[OSD([sQuery(id+"F3.wireOp",EDGE,"E20.1")])]})]});
            var Q24;
            Q24=makeQuery(id+"F4.boolean.opBoolean","INTERSECT",EDGE,{"derivedFrom":[makeQuery(id+"F1.opExtrude","CAP_FACE",FACE,{"disambiguationData":[OSD([sQuery(id+"F0.wireOp",EDGE,"E0"),sQuery(id+"F0.wireOp",EDGE,"E5.0"),sQuery(id+"F0.wireOp",EDGE,"E5.1"),sQuery(id+"F0.wireOp",EDGE,"E5.2"),sQuery(id+"F0.wireOp",EDGE,"E5.3"),sQuery(id+"F0.wireOp",EDGE,"E5.4"),sQuery(id+"F0.wireOp",EDGE,"E5.5"),sQuery(id+"F0.wireOp",EDGE,"E6.0"),sQuery(id+"F0.wireOp",EDGE,"E6.1"),sQuery(id+"F0.wireOp",EDGE,"E6.2"),sQuery(id+"F0.wireOp",EDGE,"E6.3"),sQuery(id+"F0.wireOp",EDGE,"E6.4"),sQuery(id+"F0.wireOp",EDGE,"E6.5"),sQuery(id+"F0.wireOp",EDGE,"E7.0"),sQuery(id+"F0.wireOp",EDGE,"E7.1"),sQuery(id+"F0.wireOp",EDGE,"E7.2"),sQuery(id+"F0.wireOp",EDGE,"E7.3"),sQuery(id+"F0.wireOp",EDGE,"E7.4"),sQuery(id+"F0.wireOp",EDGE,"E7.5"),sQuery(id+"F0.wireOp",EDGE,"E8"),sQuery(id+"F0.wireOp",EDGE,"E9"),sQuery(id+"F0.wireOp",EDGE,"E10"),sQuery(id+"F0.wireOp",EDGE,"E11"),sQuery(id+"F0.wireOp",EDGE,"E13"),sQuery(id+"F0.wireOp",EDGE,"E14")])],"isStart":true}),makeQuery(id+"F4.opExtrude","SWEPT_FACE",FACE,{"disambiguationData":[OSD([sQuery(id+"F3.wireOp",EDGE,"E20.0")])]})]});
            var Q25;
            Q25=makeQuery(id+"F1.opExtrude","CAP_EDGE",EDGE,{"disambiguationData":[OSD([sQuery(id+"F0.wireOp",EDGE,"E0")])],"isStart":true});
            fillet(context, id + "F6", {"entities" : qUnion([Q0, Q1, Q2, Q3, Q4, Q5, Q6, Q7, Q8, Q9, Q10, Q11, Q12, Q13, Q14, Q15, Q16, Q17, Q18, Q19, Q20, Q21, Q22, Q23, Q24, Q25]), "radius" : 1.5 * mm, "tangentPropagation" : true, "allowEdgeOverflow" : false});
        }
        {
            var Q0;
            Q0=makeQuery(id+"F4.boolean.opBoolean","INTERSECT",EDGE,{"derivedFrom":[makeQuery(id+"F1.opExtrude","CAP_FACE",FACE,{"disambiguationData":[OSD([sQuery(id+"F0.wireOp",EDGE,"E0"),sQuery(id+"F0.wireOp",EDGE,"E5.0"),sQuery(id+"F0.wireOp",EDGE,"E5.1"),sQuery(id+"F0.wireOp",EDGE,"E5.2"),sQuery(id+"F0.wireOp",EDGE,"E5.3"),sQuery(id+"F0.wireOp",EDGE,"E5.4"),sQuery(id+"F0.wireOp",EDGE,"E5.5"),sQuery(id+"F0.wireOp",EDGE,"E6.0"),sQuery(id+"F0.wireOp",EDGE,"E6.1"),sQuery(id+"F0.wireOp",EDGE,"E6.2"),sQuery(id+"F0.wireOp",EDGE,"E6.3"),sQuery(id+"F0.wireOp",EDGE,"E6.4"),sQuery(id+"F0.wireOp",EDGE,"E6.5"),sQuery(id+"F0.wireOp",EDGE,"E7.0"),sQuery(id+"F0.wireOp",EDGE,"E7.1"),sQuery(id+"F0.wireOp",EDGE,"E7.2"),sQuery(id+"F0.wireOp",EDGE,"E7.3"),sQuery(id+"F0.wireOp",EDGE,"E7.4"),sQuery(id+"F0.wireOp",EDGE,"E7.5"),sQuery(id+"F0.wireOp",EDGE,"E8"),sQuery(id+"F0.wireOp",EDGE,"E9"),sQuery(id+"F0.wireOp",EDGE,"E10"),sQuery(id+"F0.wireOp",EDGE,"E11"),sQuery(id+"F0.wireOp",EDGE,"E13"),sQuery(id+"F0.wireOp",EDGE,"E14")])],"isStart":true}),makeQuery(id+"F4.opExtrude","SWEPT_FACE",FACE,{"disambiguationData":[OSD([sQuery(id+"F3.wireOp",EDGE,"E39.trimOffspring")])]})]});
            var Q1;
            Q1=makeQuery(id+"F4.boolean.opBoolean","INTERSECT",EDGE,{"derivedFrom":[makeQuery(id+"F1.opExtrude","CAP_FACE",FACE,{"disambiguationData":[OSD([sQuery(id+"F0.wireOp",EDGE,"E0"),sQuery(id+"F0.wireOp",EDGE,"E5.0"),sQuery(id+"F0.wireOp",EDGE,"E5.1"),sQuery(id+"F0.wireOp",EDGE,"E5.2"),sQuery(id+"F0.wireOp",EDGE,"E5.3"),sQuery(id+"F0.wireOp",EDGE,"E5.4"),sQuery(id+"F0.wireOp",EDGE,"E5.5"),sQuery(id+"F0.wireOp",EDGE,"E6.0"),sQuery(id+"F0.wireOp",EDGE,"E6.1"),sQuery(id+"F0.wireOp",EDGE,"E6.2"),sQuery(id+"F0.wireOp",EDGE,"E6.3"),sQuery(id+"F0.wireOp",EDGE,"E6.4"),sQuery(id+"F0.wireOp",EDGE,"E6.5"),sQuery(id+"F0.wireOp",EDGE,"E7.0"),sQuery(id+"F0.wireOp",EDGE,"E7.1"),sQuery(id+"F0.wireOp",EDGE,"E7.2"),sQuery(id+"F0.wireOp",EDGE,"E7.3"),sQuery(id+"F0.wireOp",EDGE,"E7.4"),sQuery(id+"F0.wireOp",EDGE,"E7.5"),sQuery(id+"F0.wireOp",EDGE,"E8"),sQuery(id+"F0.wireOp",EDGE,"E9"),sQuery(id+"F0.wireOp",EDGE,"E10"),sQuery(id+"F0.wireOp",EDGE,"E11"),sQuery(id+"F0.wireOp",EDGE,"E13"),sQuery(id+"F0.wireOp",EDGE,"E14")])],"isStart":true}),makeQuery(id+"F4.opExtrude","SWEPT_FACE",FACE,{"disambiguationData":[OSD([sQuery(id+"F3.wireOp",EDGE,"E53.trimOffspring")])]})]});
            var Q2;
            Q2=makeQuery(id+"F4.boolean.opBoolean","INTERSECT",EDGE,{"derivedFrom":[makeQuery(id+"F1.opExtrude","CAP_FACE",FACE,{"disambiguationData":[OSD([sQuery(id+"F0.wireOp",EDGE,"E0"),sQuery(id+"F0.wireOp",EDGE,"E5.0"),sQuery(id+"F0.wireOp",EDGE,"E5.1"),sQuery(id+"F0.wireOp",EDGE,"E5.2"),sQuery(id+"F0.wireOp",EDGE,"E5.3"),sQuery(id+"F0.wireOp",EDGE,"E5.4"),sQuery(id+"F0.wireOp",EDGE,"E5.5"),sQuery(id+"F0.wireOp",EDGE,"E6.0"),sQuery(id+"F0.wireOp",EDGE,"E6.1"),sQuery(id+"F0.wireOp",EDGE,"E6.2"),sQuery(id+"F0.wireOp",EDGE,"E6.3"),sQuery(id+"F0.wireOp",EDGE,"E6.4"),sQuery(id+"F0.wireOp",EDGE,"E6.5"),sQuery(id+"F0.wireOp",EDGE,"E7.0"),sQuery(id+"F0.wireOp",EDGE,"E7.1"),sQuery(id+"F0.wireOp",EDGE,"E7.2"),sQuery(id+"F0.wireOp",EDGE,"E7.3"),sQuery(id+"F0.wireOp",EDGE,"E7.4"),sQuery(id+"F0.wireOp",EDGE,"E7.5"),sQuery(id+"F0.wireOp",EDGE,"E8"),sQuery(id+"F0.wireOp",EDGE,"E9"),sQuery(id+"F0.wireOp",EDGE,"E10"),sQuery(id+"F0.wireOp",EDGE,"E11"),sQuery(id+"F0.wireOp",EDGE,"E13"),sQuery(id+"F0.wireOp",EDGE,"E14")])],"isStart":true}),makeQuery(id+"F4.opExtrude","SWEPT_FACE",FACE,{"disambiguationData":[OSD([sQuery(id+"F3.wireOp",EDGE,"E22")])]})]});
            var Q3;
            Q3=makeQuery(id+"F4.boolean.opBoolean","COPY",EDGE,{"derivedFrom":makeQuery(id+"F4.opExtrude","CAP_EDGE",EDGE,{"disambiguationData":[OSD([sQuery(id+"F3.wireOp",EDGE,"E22")])],"isStart":true})});
            var Q4;
            Q4=makeQuery(id+"F4.boolean.opBoolean","COPY",EDGE,{"derivedFrom":makeQuery(id+"F4.opExtrude","CAP_EDGE",EDGE,{"disambiguationData":[OSD([sQuery(id+"F3.wireOp",EDGE,"E39.trimOffspring")])],"isStart":true})});
            var Q5;
            Q5=makeQuery(id+"F4.boolean.opBoolean","COPY",EDGE,{"derivedFrom":makeQuery(id+"F4.opExtrude","CAP_EDGE",EDGE,{"disambiguationData":[OSD([sQuery(id+"F3.wireOp",EDGE,"E53.trimOffspring")])],"isStart":true})});
            fillet(context, id + "F7", {"entities" : qUnion([Q0, Q1, Q2, Q3, Q4, Q5]), "radius" : 1 * mm, "tangentPropagation" : true, "allowEdgeOverflow" : false});
        }
    });
